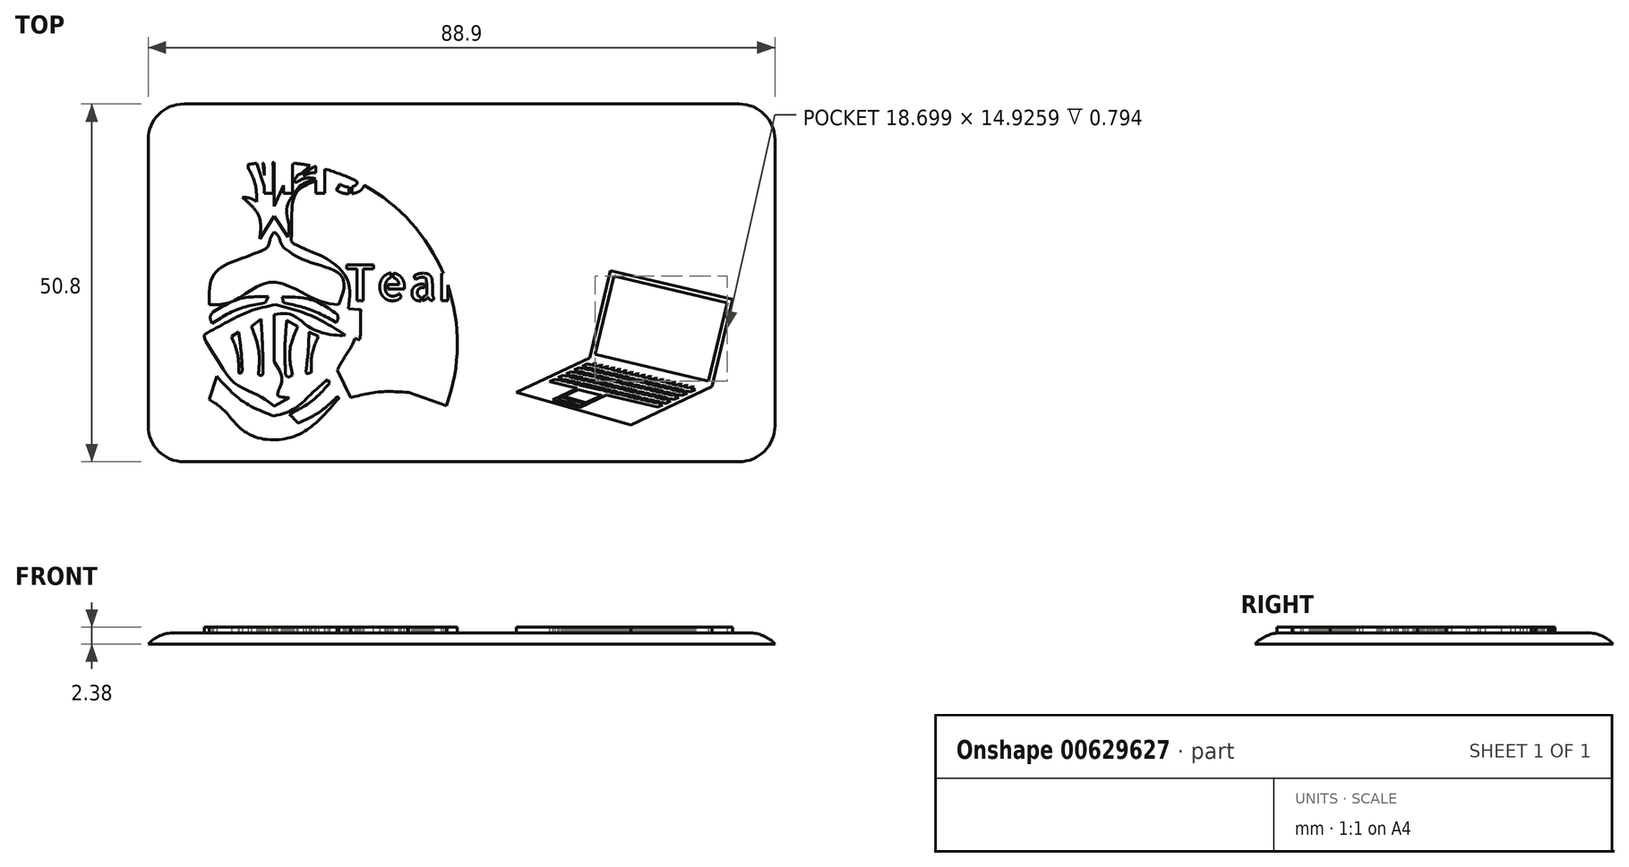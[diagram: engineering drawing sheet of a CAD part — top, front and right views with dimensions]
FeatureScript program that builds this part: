
annotation { "Feature Type Name" : "Feature", "Feature Type Description" : "" }
export const myFeature = defineFeature(function(context is Context, id is Id, definition is map)
    precondition{}
    {
        {
            var Q0;
            Q0=qCreatedBy(makeId("Top.planeOp"),FACE);
            var sketch = newSketch(context, id + "F0", { "sketchPlane" : qUnion([Q0])});
            skLineSegment(sketch, "E0.bottom", {"start": v(-44.45, 25.4) * mm, "end": v(44.45, 25.4) * mm});
            skLineSegment(sketch, "E0.top", {"start": v(-44.45, -25.4) * mm, "end": v(44.45, -25.4) * mm});
            skLineSegment(sketch, "E0.left", {"start": v(-44.45, 25.4) * mm, "end": v(-44.45, -25.4) * mm});
            skLineSegment(sketch, "E0.right", {"start": v(44.45, 25.4) * mm, "end": v(44.45, -25.4) * mm});
            skPoint(sketch, "E0.middle", {"position": v(0, 0) * mm});
            skSolve(sketch);
        }
        {
            var Q0;
            Q0=qSketchRegion(id+"F0",true);
            extrude(context, id + "F1", {"entities" : qUnion([Q0]), "depth" : 1.59 * mm, "offsetDistance" : 25.4 * mm});
        }
        {
            var Q0;
            {var subQ0=sQuery(id+"F0.wireOp",EDGE,"E0.right");var subQ1=sQuery(id+"F0.wireOp",EDGE,"E0.left");var subQ2=sQuery(id+"F0.wireOp",EDGE,"E0.top");var subQ3=sQuery(id+"F0.wireOp",EDGE,"E0.bottom");var subQ4=makeQuery(id+"F1.opExtrude","CAP_FACE",FACE,{"disambiguationData":[OSD([subQ3,subQ2,subQ1,subQ0])],"isStart":false});Q0=makeQuery(id+"F5.boolean.opBoolean","SPLIT",FACE,{"disambiguationData":[TD([makeQuery(id+"F7.boolean.opBoolean","COPY",FACE,{"derivedFrom":makeQuery(id+"F7.opExtrude","SWEPT_FACE",FACE,{"disambiguationData":[OSD([sQuery(id+"F6.wireOp",EDGE,"E188.sketch_text.stroke-0")])]})})])],"derivedFrom":subQ4});}
            var sketch = newSketch(context, id + "F2", { "sketchPlane" : qUnion([Q0])});
            skLineSegment(sketch, "E1", {"start": v(-39.93, 20.88) * mm, "end": v(-39.93, 13.23) * mm});
            skLineSegment(sketch, "E2", {"start": v(-39.93, 20.88) * mm, "end": v(-39.12, 20.88) * mm});
            skLineSegment(sketch, "E3", {"start": v(-37.79, -20.88) * mm, "end": v(-35.63, -20.88) * mm});
            skLineSegment(sketch, "E4.0", {"start": v(-11.09, 20.88) * mm, "end": v(-6.97, 18.68) * mm});
            skLineSegment(sketch, "E4.1", {"start": v(-14.12, 20.88) * mm, "end": v(-16.69, 18.68) * mm});
            skLineSegment(sketch, "E4.13", {"start": v(2.67, -20.88) * mm, "end": v(0.61, -18.26) * mm});
            skLineSegment(sketch, "E4.14", {"start": v(0.36, 11.02) * mm, "end": v(3.83, 4.92) * mm});
            skLineSegment(sketch, "E4.15", {"start": v(0.36, 11.02) * mm, "end": v(-4.42, 10.07) * mm});
            skArc(sketch, "E4.16", {"start": v(-4.42, 10.07) * mm, "mid": v(-5.98, 11.8) * mm, "end": v(-7.68, 13.38) * mm});
            skLineSegment(sketch, "E4.17", {"start": v(-6.97, 18.68) * mm, "end": v(-7.68, 13.38) * mm});
            skLineSegment(sketch, "E4.18", {"start": v(3.83, 4.92) * mm, "end": v(0.61, 1.3) * mm});
            skArc(sketch, "E4.19", {"start": v(1.92, -3.68) * mm, "mid": v(1.38, -1.16) * mm, "end": v(0.61, 1.3) * mm});
            skLineSegment(sketch, "E4.20", {"start": v(6.61, -5.16) * mm, "end": v(1.92, -3.68) * mm});
            skLineSegment(sketch, "E4.21", {"start": v(6.61, -5.16) * mm, "end": v(6.61, -11.77) * mm});
            skLineSegment(sketch, "E4.22", {"start": v(6.61, -11.77) * mm, "end": v(1.92, -13.28) * mm});
            skArc(sketch, "E4.23", {"start": v(0.61, -18.26) * mm, "mid": v(1.38, -15.8) * mm, "end": v(1.92, -13.28) * mm});
            skLineSegment(sketch, "E4.42", {"start": v(-39.12, 20.88) * mm, "end": v(-36.5, 18.68) * mm});
            skArc(sketch, "E4.43", {"start": v(-31.89, 19.94) * mm, "mid": v(-34.22, 19.4) * mm, "end": v(-36.5, 18.68) * mm});
            skLineSegment(sketch, "E4.44", {"start": v(-31.89, 19.94) * mm, "end": v(-31.5, 20.88) * mm});
            skLineSegment(sketch, "E4.46", {"start": v(-21.66, 20.88) * mm, "end": v(-21.3, 19.94) * mm});
            skArc(sketch, "E4.47", {"start": v(-16.69, 18.68) * mm, "mid": v(-18.96, 19.4) * mm, "end": v(-21.3, 19.94) * mm});
            skLineSegment(sketch, "E5.0", {"start": v(-17.63, -12.4) * mm, "end": v(-15.7, -16.29) * mm});
            skFitSpline(sketch, "E5.1", {"points": [v(-7.65, -15.55) * mm, v(-11.69, -15.5) * mm, v(-15.7, -16.29) * mm]});
            skLineSegment(sketch, "E5.2", {"start": v(-7.65, -15.55) * mm, "end": v(-7.5, -15.55) * mm});
            skLineSegment(sketch, "E5.3", {"start": v(-16.04, -3.68) * mm, "end": v(-14.6, -3.8) * mm});
            skFitSpline(sketch, "E5.4", {"points": [v(-14.36, -4.47) * mm, v(-14.33, -4.23) * mm, v(-14.32, -3.82) * mm, v(-14.6, -3.8) * mm]});
            skLineSegment(sketch, "E5.5", {"start": v(-14.36, -4.47) * mm, "end": v(-14.36, -7.44) * mm});
            skFitSpline(sketch, "E5.6", {"points": [v(-15.13, -7.93) * mm, v(-14.83, -7.99) * mm, v(-14.54, -8.08) * mm, v(-14.36, -7.44) * mm]});
            skFitSpline(sketch, "E5.7", {"points": [v(-16.04, -3.68) * mm, v(-16.1, 0.17) * mm, v(-19.42, 3.57) * mm, v(-23.98, 5.7) * mm, v(-24.16, 6.21) * mm]});
            skFitSpline(sketch, "E5.8", {"points": [v(-24.16, 6.21) * mm, v(-24.11, 7.19) * mm, v(-23.98, 11.28) * mm, v(-22.96, 13.3) * mm, v(-19.48, 14.97) * mm]});
            skFitSpline(sketch, "E5.9", {"points": [v(-19.48, 14.97) * mm, v(-20.81, 15.64) * mm, v(-22.46, 15.17) * mm]});
            skFitSpline(sketch, "E5.10", {"points": [v(-17.63, -12.4) * mm, v(-16.8, -10.89) * mm, v(-15.86, -9.46) * mm, v(-15.13, -7.93) * mm]});
            skFitSpline(sketch, "E5.11", {"points": [v(-22.46, 15.17) * mm, v(-21.72, 15.9) * mm, v(-20.87, 16.52) * mm]});
            skArc(sketch, "E5.12", {"start": v(-2.15, -17.45) * mm, "mid": v(-3.8, 3.8) * mm, "end": v(-20.87, 16.52) * mm});
            skLineSegment(sketch, "E5.13", {"start": v(-7.5, -15.55) * mm, "end": v(-2.15, -17.45) * mm});
            skArc(sketch, "E6.0", {"start": v(-31.1, 16.66) * mm, "mid": v(-35.68, 15.36) * mm, "end": v(-39.93, 13.23) * mm});
            skLineSegment(sketch, "E6.2", {"start": v(-38.12, -3.8) * mm, "end": v(-37.08, -3.8) * mm});
            skFitSpline(sketch, "E6.3", {"points": [v(-29.04, 5.91) * mm, v(-32.6, 3.54) * mm, v(-36.03, 3.27) * mm, v(-37.08, -3.8) * mm]});
            skFitSpline(sketch, "E6.4", {"points": [v(-32.5, 12.72) * mm, v(-29.26, 10.64) * mm, v(-29.04, 5.91) * mm]});
            skFitSpline(sketch, "E6.5", {"points": [v(-29.6, 12.07) * mm, v(-30.83, 12.9) * mm, v(-32.5, 12.72) * mm]});
            skFitSpline(sketch, "E6.6", {"points": [v(-38.12, -3.8) * mm, v(-38.46, -3.77) * mm, v(-38.6, -3.99) * mm, v(-38.6, -4.15) * mm]});
            skLineSegment(sketch, "E6.7", {"start": v(-38.6, -7.34) * mm, "end": v(-38.6, -4.15) * mm});
            skFitSpline(sketch, "E6.8", {"points": [v(-31.1, 16.66) * mm, v(-30.26, 15.3) * mm, v(-29.66, 13.77) * mm, v(-29.6, 12.07) * mm]});
            skFitSpline(sketch, "E6.9", {"points": [v(-38.6, -7.34) * mm, v(-38.84, -7.76) * mm, v(-38.04, -8) * mm]});
            skFitSpline(sketch, "E6.10", {"points": [v(-38.04, -8) * mm, v(-36.8, -10.21) * mm, v(-35.5, -12.4) * mm]});
            skLineSegment(sketch, "E6.11", {"start": v(-37.39, -16.29) * mm, "end": v(-35.5, -12.4) * mm});
            skFitSpline(sketch, "E6.12", {"points": [v(-37.39, -16.29) * mm, v(-41.55, -15.61) * mm, v(-45.73, -15.55) * mm]});
            skLineSegment(sketch, "E7.0", {"start": v(-33.08, -20.88) * mm, "end": v(-35.5, -19.2) * mm});
            skLineSegment(sketch, "E7.1", {"start": v(-35.5, -19.2) * mm, "end": v(-35.63, -20.88) * mm});
            skArc(sketch, "E8.1", {"start": v(-3.7, -20.88) * mm, "mid": v(-3.07, -19.66) * mm, "end": v(-2.52, -18.4) * mm});
            skLineSegment(sketch, "E8.2", {"start": v(-16.04, -18.26) * mm, "end": v(-15.47, -20.88) * mm});
            skFitSpline(sketch, "E8.3", {"points": [v(-16.04, -18.26) * mm, v(-16.15, -17.79) * mm, v(-15.43, -17.5) * mm]});
            skLineSegment(sketch, "E8.4", {"start": v(-7.5, -16.6) * mm, "end": v(-15.43, -17.5) * mm});
            skLineSegment(sketch, "E8.6", {"start": v(-2.52, -18.4) * mm, "end": v(-7.5, -16.6) * mm});
            skLineSegment(sketch, "E9.0", {"start": v(-37.39, -17.54) * mm, "end": v(-39.93, -17.25) * mm});
            skLineSegment(sketch, "E9.1", {"start": v(-37.79, -20.88) * mm, "end": v(-37.39, -18.92) * mm});
            skFitSpline(sketch, "E9.3", {"points": [v(-37.39, -17.54) * mm, v(-37.1, -18.3) * mm, v(-37.39, -18.92) * mm]});
            skFitSpline(sketch, "E10.0", {"points": [v(-23.19, -19.91) * mm, v(-20.18, -18.37) * mm, v(-17.6, -16.11) * mm]});
            skFitSpline(sketch, "E10.1", {"points": [v(-23.19, -19.91) * mm, v(-23.5, -19.6) * mm, v(-23.9, -19.16) * mm, v(-24.45, -18.66) * mm]});
            skFitSpline(sketch, "E10.2", {"points": [v(-17.6, -16.11) * mm, v(-17.44, -16.44) * mm, v(-17.63, -16.6) * mm]});
            skFitSpline(sketch, "E10.3", {"points": [v(-18.7, -14.2) * mm, v(-21.24, -16.8) * mm, v(-24.45, -18.66) * mm]});
            skLineSegment(sketch, "E10.4", {"start": v(-18.7, -14.2) * mm, "end": v(-18.94, -13.74) * mm});
            skFitSpline(sketch, "E10.5", {"points": [v(-17.63, -16.6) * mm, v(-19.85, -19.09) * mm, v(-22.95, -21.46) * mm, v(-27.12, -22.28) * mm, v(-31.04, -20.92) * mm, v(-33.86, -17.94) * mm, v(-35.78, -16.6) * mm]});
            skLineSegment(sketch, "E10.6", {"start": v(-34.7, -13.28) * mm, "end": v(-35.78, -16.6) * mm});
            skFitSpline(sketch, "E10.7", {"points": [v(-26.6, -18.92) * mm, v(-31.06, -16.8) * mm, v(-34.7, -13.28) * mm]});
            skFitSpline(sketch, "E10.8", {"points": [v(-18.94, -13.74) * mm, v(-21.29, -15.73) * mm, v(-23.66, -17.85) * mm, v(-26.6, -18.92) * mm]});
            skFitSpline(sketch, "E11.0", {"points": [v(-26.6, -17.54) * mm, v(-28.47, -16.2) * mm, v(-32.14, -14.27) * mm, v(-34.18, -11.66) * mm, v(-36.38, -8.05) * mm, v(-36.5, -7.34) * mm]});
            skLineSegment(sketch, "E11.1", {"start": v(-26.6, -17.54) * mm, "end": v(-24.45, -16.29) * mm});
            skFitSpline(sketch, "E11.2", {"points": [v(-26.34, -3.1) * mm, v(-21.2, -4.73) * mm, v(-16.46, -7.44) * mm]});
            skFitSpline(sketch, "E11.3", {"points": [v(-16.46, -7.44) * mm, v(-17.65, -7.44) * mm, v(-21.16, -6.55) * mm, v(-24.06, -4.55) * mm, v(-26.56, -4.47) * mm]});
            skLineSegment(sketch, "E11.4", {"start": v(-26.56, -11.18) * mm, "end": v(-26.56, -4.47) * mm});
            skFitSpline(sketch, "E11.5", {"points": [v(-36.5, -7.34) * mm, v(-33.28, -5.58) * mm, v(-29.94, -4) * mm, v(-26.34, -3.1) * mm]});
            skFitSpline(sketch, "E11.6", {"points": [v(-26.56, -11.18) * mm, v(-25.5, -14.07) * mm, v(-26.07, -15.95) * mm, v(-24.45, -16.29) * mm]});
            skFitSpline(sketch, "E12.0", {"points": [v(-29.8, -6.2) * mm, v(-28.78, -9.6) * mm, v(-28.81, -13.06) * mm]});
            skLineSegment(sketch, "E12.1", {"start": v(-28.45, -5.16) * mm, "end": v(-29.8, -6.2) * mm});
            skFitSpline(sketch, "E12.2", {"points": [v(-28.17, -12.77) * mm, v(-28.23, -8.96) * mm, v(-28.45, -5.16) * mm]});
            skFitSpline(sketch, "E12.3", {"points": [v(-28.81, -13.06) * mm, v(-28.3, -13.1) * mm, v(-28.17, -12.77) * mm]});
            skFitSpline(sketch, "E13.0", {"points": [v(-31.61, -12.77) * mm, v(-31.3, -12.82) * mm, v(-31.1, -12.4) * mm]});
            skFitSpline(sketch, "E13.1", {"points": [v(-32.64, -7.63) * mm, v(-31.76, -10.15) * mm, v(-31.61, -12.77) * mm]});
            skLineSegment(sketch, "E13.2", {"start": v(-31.61, -6.96) * mm, "end": v(-32.64, -7.63) * mm});
            skFitSpline(sketch, "E13.3", {"points": [v(-31.1, -12.4) * mm, v(-31.28, -9.67) * mm, v(-31.61, -6.96) * mm]});
            skFitSpline(sketch, "E14.0", {"points": [v(-25, -12.77) * mm, v(-24.92, -13.1) * mm, v(-24.52, -13.36) * mm, v(-23.99, -13.06) * mm]});
            skFitSpline(sketch, "E14.1", {"points": [v(-25, -12.77) * mm, v(-25.05, -9.05) * mm, v(-24.8, -5.34) * mm]});
            skLineSegment(sketch, "E14.2", {"start": v(-23.19, -6.2) * mm, "end": v(-24.8, -5.34) * mm});
            skFitSpline(sketch, "E14.3", {"points": [v(-23.99, -13.06) * mm, v(-24.35, -9.62) * mm, v(-23.19, -6.2) * mm]});
            skFitSpline(sketch, "E15.0", {"points": [v(-21.3, -12.77) * mm, v(-21.41, -12.73) * mm, v(-21.9, -12.9) * mm, v(-22.07, -12.52) * mm]});
            skFitSpline(sketch, "E15.1", {"points": [v(-21.3, -12.77) * mm, v(-21.22, -10.15) * mm, v(-20.3, -7.63) * mm]});
            skLineSegment(sketch, "E15.2", {"start": v(-20.3, -7.63) * mm, "end": v(-21.64, -6.96) * mm});
            skFitSpline(sketch, "E15.3", {"points": [v(-22.07, -12.52) * mm, v(-21.76, -9.75) * mm, v(-21.64, -6.96) * mm]});
            skFitSpline(sketch, "E16.0", {"points": [v(-27.86, -2.82) * mm, v(-31.79, -3.78) * mm, v(-35.38, -5.78) * mm]});
            skLineSegment(sketch, "E16.1", {"start": v(-27.86, -2.82) * mm, "end": v(-27.44, -1.99) * mm});
            skFitSpline(sketch, "E16.2", {"points": [v(-27.44, -1.99) * mm, v(-31.46, -2.27) * mm, v(-35.22, -4.15) * mm]});
            skFitSpline(sketch, "E16.3", {"points": [v(-35.38, -5.78) * mm, v(-35.64, -4.85) * mm, v(-35.22, -4.15) * mm]});
            skFitSpline(sketch, "E17.0", {"points": [v(-25.24, -2.82) * mm, v(-21.38, -3.85) * mm, v(-17.74, -5.62) * mm]});
            skLineSegment(sketch, "E17.1", {"start": v(-25.46, -1.99) * mm, "end": v(-25.24, -2.82) * mm});
            skFitSpline(sketch, "E17.2", {"points": [v(-17.63, -4.47) * mm, v(-21.2, -2.44) * mm, v(-25.46, -1.99) * mm]});
            skFitSpline(sketch, "E17.3", {"points": [v(-17.74, -5.62) * mm, v(-17.54, -5.08) * mm, v(-17.63, -4.47) * mm]});
            skLineSegment(sketch, "E18.0", {"start": v(-21.64, 16.53) * mm, "end": v(-21.52, 16.66) * mm});
            skArc(sketch, "E18.1", {"start": v(-21.52, 16.66) * mm, "mid": v(-22.69, 16.85) * mm, "end": v(-23.87, 17) * mm});
            skLineSegment(sketch, "E18.2", {"start": v(-23.87, 17) * mm, "end": v(-26.6, 10.84) * mm});
            skLineSegment(sketch, "E18.3", {"start": v(-26.6, 10.84) * mm, "end": v(-26.6, 17.1) * mm});
            skArc(sketch, "E18.4", {"start": v(-26.6, 17.1) * mm, "mid": v(-27.38, 17.09) * mm, "end": v(-28.17, 17.04) * mm});
            skFitSpline(sketch, "E18.5", {"points": [v(-21.64, 16.53) * mm, v(-22.97, 15.4) * mm, v(-23.04, 15.44) * mm, v(-23.74, 14.42) * mm, v(-23.43, 14.3) * mm]});
            skLineSegment(sketch, "E18.6", {"start": v(-28.17, 17.04) * mm, "end": v(-27.72, 12.88) * mm});
            skLineSegment(sketch, "E18.7", {"start": v(-26.6, 9.5) * mm, "end": v(-24.6, 6.5) * mm});
            skFitSpline(sketch, "E18.8", {"points": [v(-20.66, 14.78) * mm, v(-22.53, 14.03) * mm, v(-23.6, 12.91) * mm, v(-24.83, 10.42) * mm, v(-24.5, 8.42) * mm, v(-24.6, 6.5) * mm]});
            skFitSpline(sketch, "E18.9", {"points": [v(-23.39, 14.3) * mm, v(-22.04, 14.87) * mm, v(-20.66, 14.78) * mm]});
            skLineSegment(sketch, "E18.10", {"start": v(-23.39, 14.3) * mm, "end": v(-23.43, 14.3) * mm});
            skLineSegment(sketch, "E18.11", {"start": v(-28.64, 6.21) * mm, "end": v(-26.6, 9.5) * mm});
            skFitSpline(sketch, "E18.12", {"points": [v(-28.64, 6.21) * mm, v(-28.74, 9.43) * mm, v(-31.1, 12.15) * mm]});
            skFitSpline(sketch, "E18.13", {"points": [v(-31.1, 12.15) * mm, v(-30.03, 12.01) * mm, v(-29.04, 11.5) * mm]});
            skFitSpline(sketch, "E18.14", {"points": [v(-29.04, 11.5) * mm, v(-29.32, 14.22) * mm, v(-30.54, 16.77) * mm]});
            skArc(sketch, "E18.15", {"start": v(-29.04, 16.97) * mm, "mid": v(-29.79, 16.88) * mm, "end": v(-30.54, 16.77) * mm});
            skLineSegment(sketch, "E18.16", {"start": v(-27.72, 12.88) * mm, "end": v(-29.04, 16.97) * mm});
            skFitSpline(sketch, "E19.0", {"points": [v(-35.78, -3.1) * mm, v(-35.06, 1.3) * mm, v(-31.74, 3.25) * mm, v(-28.45, 4.52) * mm]});
            skFitSpline(sketch, "E20.0", {"points": [v(-28.45, 4.52) * mm, v(-27.52, 5.12) * mm, v(-27.11, 6.28) * mm, v(-26.6, 7.24) * mm]});
            skFitSpline(sketch, "E21.0", {"points": [v(-25.15, 4.92) * mm, v(-21.92, 3.09) * mm, v(-16.98, 0.88) * mm, v(-17.42, -3.1) * mm]});
            skFitSpline(sketch, "E21.1", {"points": [v(-26.6, 7.24) * mm, v(-25.96, 6.59) * mm, v(-25.67, 5.71) * mm, v(-25.15, 4.92) * mm]});
            skFitSpline(sketch, "E22.0", {"points": [v(-35.78, -3.1) * mm, v(-32.32, -2.55) * mm, v(-26.97, 0.08) * mm, v(-20.8, -2.33) * mm, v(-17.42, -3.1) * mm]});
            skLineSegment(sketch, "E23.trimOffspring", {"start": v(-39.93, -15.93) * mm, "end": v(-39.93, -17.25) * mm});
            skLineSegment(sketch, "E24.trimOffspring", {"start": v(-33.08, -20.88) * mm, "end": v(-30.2, -20.88) * mm});
            skFitSpline(sketch, "E25.trimOffspring", {"points": [v(-17.63, -16.6) * mm, v(-19.85, -19.09) * mm, v(-22.95, -21.46) * mm, v(-27.12, -22.28) * mm, v(-31.04, -20.92) * mm, v(-33.86, -17.94) * mm, v(-35.78, -16.6) * mm]});
            skLineSegment(sketch, "E26.trimOffspring", {"start": v(-22.9, -20.88) * mm, "end": v(-15.47, -20.88) * mm});
            skLineSegment(sketch, "E27.trimOffspring", {"start": v(-3.7, -20.88) * mm, "end": v(2.67, -20.88) * mm});
            skPoint(sketch, "E28.orphan", {"position": v(87.07, -20.88) * mm});
            skLineSegment(sketch, "E29.trimOffspring", {"start": v(-31.5, 20.88) * mm, "end": v(-21.66, 20.88) * mm});
            skPoint(sketch, "E30.orphan", {"position": v(48.02, 20.88) * mm});
            skLineSegment(sketch, "E31.trimOffspring", {"start": v(-14.12, 20.88) * mm, "end": v(-11.09, 20.88) * mm});
            skSolve(sketch);
        }
        {
            var Q0;
            Q0=qSketchRegion(id+"F2",true);
            extrude(context, id + "F3", {"entities" : qUnion([Q0]), "operationType" : NewBodyOperationType.ADD, "depth" : 0.8 * mm, "offsetDistance" : 25.4 * mm});
        }
        {
            var Q0;
            Q0=makeQuery(id+"F1.opExtrude","CAP_FACE",FACE,{"disambiguationData":[OSD([sQuery(id+"F0.wireOp",EDGE,"E0.bottom"),sQuery(id+"F0.wireOp",EDGE,"E0.top"),sQuery(id+"F0.wireOp",EDGE,"E0.left"),sQuery(id+"F0.wireOp",EDGE,"E0.right")])],"isStart":false});
            var sketch = newSketch(context, id + "F4", { "sketchPlane" : qUnion([Q0])});
            skLineSegment(sketch, "E32", {"start": v(-33.18, -82.37) * mm, "end": v(-27.78, -81.02) * mm});
            skLineSegment(sketch, "E33", {"start": v(24.02, -20.16) * mm, "end": v(35.5, -14.73) * mm});
            skLineSegment(sketch, "E34", {"start": v(35.5, -14.73) * mm, "end": v(38.42, -2.37) * mm});
            skLineSegment(sketch, "E35", {"start": v(38.42, -2.37) * mm, "end": v(21.12, 1.72) * mm});
            skLineSegment(sketch, "E36", {"start": v(21.12, 1.72) * mm, "end": v(18.2, -10.63) * mm});
            skLineSegment(sketch, "E37", {"start": v(18.2, -10.63) * mm, "end": v(35.5, -14.73) * mm});
            skLineSegment(sketch, "E38", {"start": v(18.2, -10.63) * mm, "end": v(7.79, -15.56) * mm});
            skLineSegment(sketch, "E39", {"start": v(7.79, -15.56) * mm, "end": v(24.02, -20.16) * mm});
            skLineSegment(sketch, "E40.0", {"start": v(18.27, -11.3) * mm, "end": v(19.13, -11.5) * mm});
            skLineSegment(sketch, "E40.1", {"start": v(17.83, -11.51) * mm, "end": v(17.12, -11.85) * mm});
            skLineSegment(sketch, "E40.2", {"start": v(13.62, -16.56) * mm, "end": v(15.08, -16.97) * mm});
            skLineSegment(sketch, "E40.3", {"start": v(27.82, -17.66) * mm, "end": v(28.56, -17.31) * mm});
            skLineSegment(sketch, "E41", {"start": v(17.83, -11.51) * mm, "end": v(18.42, -11.65) * mm});
            skLineSegment(sketch, "E42", {"start": v(18.42, -11.65) * mm, "end": v(18.86, -11.44) * mm});
            skPoint(sketch, "E43", {"position": v(17.83, -11.51) * mm});
            skPoint(sketch, "E44", {"position": v(18.27, -11.3) * mm});
            skPoint(sketch, "E45", {"position": v(18.42, -11.65) * mm});
            skPoint(sketch, "E46", {"position": v(18.86, -11.44) * mm});
            skPoint(sketch, "E47.1.0.0", {"position": v(19.13, -11.5) * mm});
            skLineSegment(sketch, "E47.1.0.1", {"start": v(18.7, -11.72) * mm, "end": v(19.28, -11.86) * mm});
            skLineSegment(sketch, "E47.1.0.2", {"start": v(19.28, -11.86) * mm, "end": v(19.72, -11.65) * mm});
            skPoint(sketch, "E47.1.0.3", {"position": v(19.28, -11.86) * mm});
            skPoint(sketch, "E47.1.0.4", {"position": v(19.72, -11.65) * mm});
            skPoint(sketch, "E47.1.0.5", {"position": v(18.7, -11.72) * mm});
            skPoint(sketch, "E47.2.0.0", {"position": v(20, -11.71) * mm});
            skLineSegment(sketch, "E47.2.0.1", {"start": v(19.56, -11.92) * mm, "end": v(20.15, -12.06) * mm});
            skLineSegment(sketch, "E47.2.0.2", {"start": v(20.15, -12.06) * mm, "end": v(20.59, -11.85) * mm});
            skPoint(sketch, "E47.2.0.3", {"position": v(20.15, -12.06) * mm});
            skPoint(sketch, "E47.2.0.4", {"position": v(20.59, -11.85) * mm});
            skPoint(sketch, "E47.2.0.5", {"position": v(19.56, -11.92) * mm});
            skPoint(sketch, "E47.3.0.0", {"position": v(20.86, -11.92) * mm});
            skLineSegment(sketch, "E47.3.0.1", {"start": v(20.42, -12.13) * mm, "end": v(21.01, -12.27) * mm});
            skLineSegment(sketch, "E47.3.0.2", {"start": v(21.01, -12.27) * mm, "end": v(21.45, -12.06) * mm});
            skPoint(sketch, "E47.3.0.3", {"position": v(21.01, -12.27) * mm});
            skPoint(sketch, "E47.3.0.4", {"position": v(21.45, -12.06) * mm});
            skPoint(sketch, "E47.3.0.5", {"position": v(20.42, -12.13) * mm});
            skPoint(sketch, "E47.4.0.0", {"position": v(21.73, -12.12) * mm});
            skLineSegment(sketch, "E47.4.0.1", {"start": v(21.29, -12.33) * mm, "end": v(21.88, -12.47) * mm});
            skLineSegment(sketch, "E47.4.0.2", {"start": v(21.88, -12.47) * mm, "end": v(22.32, -12.26) * mm});
            skPoint(sketch, "E47.4.0.3", {"position": v(21.88, -12.47) * mm});
            skPoint(sketch, "E47.4.0.4", {"position": v(22.32, -12.26) * mm});
            skPoint(sketch, "E47.4.0.5", {"position": v(21.29, -12.33) * mm});
            skPoint(sketch, "E47.5.0.0", {"position": v(22.6, -12.33) * mm});
            skLineSegment(sketch, "E47.5.0.1", {"start": v(22.15, -12.54) * mm, "end": v(22.74, -12.68) * mm});
            skLineSegment(sketch, "E47.5.0.2", {"start": v(22.74, -12.68) * mm, "end": v(23.18, -12.47) * mm});
            skPoint(sketch, "E47.5.0.3", {"position": v(22.74, -12.68) * mm});
            skPoint(sketch, "E47.5.0.4", {"position": v(23.18, -12.47) * mm});
            skPoint(sketch, "E47.5.0.5", {"position": v(22.15, -12.54) * mm});
            skPoint(sketch, "E47.6.0.0", {"position": v(23.46, -12.53) * mm});
            skLineSegment(sketch, "E47.6.0.1", {"start": v(23.02, -12.74) * mm, "end": v(23.6, -12.88) * mm});
            skLineSegment(sketch, "E47.6.0.2", {"start": v(23.6, -12.88) * mm, "end": v(24.05, -12.67) * mm});
            skPoint(sketch, "E47.6.0.3", {"position": v(23.6, -12.88) * mm});
            skPoint(sketch, "E47.6.0.4", {"position": v(24.05, -12.67) * mm});
            skPoint(sketch, "E47.6.0.5", {"position": v(23.02, -12.74) * mm});
            skPoint(sketch, "E47.7.0.0", {"position": v(24.32, -12.74) * mm});
            skLineSegment(sketch, "E47.7.0.1", {"start": v(23.88, -12.95) * mm, "end": v(24.47, -13.09) * mm});
            skLineSegment(sketch, "E47.7.0.2", {"start": v(24.47, -13.09) * mm, "end": v(24.91, -12.88) * mm});
            skPoint(sketch, "E47.7.0.3", {"position": v(24.47, -13.09) * mm});
            skPoint(sketch, "E47.7.0.4", {"position": v(24.91, -12.88) * mm});
            skPoint(sketch, "E47.7.0.5", {"position": v(23.88, -12.95) * mm});
            skPoint(sketch, "E47.8.0.0", {"position": v(25.19, -12.94) * mm});
            skLineSegment(sketch, "E47.8.0.1", {"start": v(24.75, -13.15) * mm, "end": v(25.34, -13.3) * mm});
            skLineSegment(sketch, "E47.8.0.2", {"start": v(25.34, -13.3) * mm, "end": v(25.78, -13.08) * mm});
            skPoint(sketch, "E47.8.0.3", {"position": v(25.34, -13.3) * mm});
            skPoint(sketch, "E47.8.0.4", {"position": v(25.78, -13.08) * mm});
            skPoint(sketch, "E47.8.0.5", {"position": v(24.75, -13.15) * mm});
            skPoint(sketch, "E47.9.0.0", {"position": v(26.05, -13.15) * mm});
            skLineSegment(sketch, "E47.9.0.1", {"start": v(25.61, -13.36) * mm, "end": v(26.2, -13.5) * mm});
            skLineSegment(sketch, "E47.9.0.2", {"start": v(26.2, -13.5) * mm, "end": v(26.64, -13.29) * mm});
            skPoint(sketch, "E47.9.0.3", {"position": v(26.2, -13.5) * mm});
            skPoint(sketch, "E47.9.0.4", {"position": v(26.64, -13.29) * mm});
            skPoint(sketch, "E47.9.0.5", {"position": v(25.61, -13.36) * mm});
            skPoint(sketch, "E47.10.0.0", {"position": v(26.92, -13.35) * mm});
            skLineSegment(sketch, "E47.10.0.1", {"start": v(26.48, -13.56) * mm, "end": v(27.07, -13.7) * mm});
            skLineSegment(sketch, "E47.10.0.2", {"start": v(27.07, -13.7) * mm, "end": v(27.5, -13.5) * mm});
            skPoint(sketch, "E47.10.0.3", {"position": v(27.07, -13.7) * mm});
            skPoint(sketch, "E47.10.0.4", {"position": v(27.5, -13.5) * mm});
            skPoint(sketch, "E47.10.0.5", {"position": v(26.48, -13.56) * mm});
            skPoint(sketch, "E47.11.0.0", {"position": v(27.78, -13.56) * mm});
            skLineSegment(sketch, "E47.11.0.1", {"start": v(27.34, -13.77) * mm, "end": v(27.93, -13.9) * mm});
            skLineSegment(sketch, "E47.11.0.2", {"start": v(27.93, -13.9) * mm, "end": v(28.37, -13.7) * mm});
            skPoint(sketch, "E47.11.0.3", {"position": v(27.93, -13.9) * mm});
            skPoint(sketch, "E47.11.0.4", {"position": v(28.37, -13.7) * mm});
            skPoint(sketch, "E47.11.0.5", {"position": v(27.34, -13.77) * mm});
            skPoint(sketch, "E47.12.0.0", {"position": v(28.65, -13.76) * mm});
            skLineSegment(sketch, "E47.12.0.1", {"start": v(28.2, -13.97) * mm, "end": v(28.8, -14.11) * mm});
            skLineSegment(sketch, "E47.12.0.2", {"start": v(28.8, -14.11) * mm, "end": v(29.24, -13.9) * mm});
            skPoint(sketch, "E47.12.0.3", {"position": v(28.8, -14.11) * mm});
            skPoint(sketch, "E47.12.0.4", {"position": v(29.24, -13.9) * mm});
            skPoint(sketch, "E47.12.0.5", {"position": v(28.2, -13.97) * mm});
            skPoint(sketch, "E47.13.0.0", {"position": v(29.51, -13.97) * mm});
            skLineSegment(sketch, "E47.13.0.1", {"start": v(29.07, -14.18) * mm, "end": v(29.66, -14.32) * mm});
            skLineSegment(sketch, "E47.13.0.2", {"start": v(29.66, -14.32) * mm, "end": v(30.1, -14.1) * mm});
            skPoint(sketch, "E47.13.0.3", {"position": v(29.66, -14.32) * mm});
            skPoint(sketch, "E47.13.0.4", {"position": v(30.1, -14.1) * mm});
            skPoint(sketch, "E47.13.0.5", {"position": v(29.07, -14.18) * mm});
            skPoint(sketch, "E47.14.0.0", {"position": v(30.38, -14.17) * mm});
            skLineSegment(sketch, "E47.14.0.1", {"start": v(29.94, -14.38) * mm, "end": v(30.53, -14.52) * mm});
            skLineSegment(sketch, "E47.14.0.2", {"start": v(30.53, -14.52) * mm, "end": v(30.97, -14.31) * mm});
            skPoint(sketch, "E47.14.0.3", {"position": v(30.53, -14.52) * mm});
            skPoint(sketch, "E47.14.0.4", {"position": v(30.97, -14.31) * mm});
            skPoint(sketch, "E47.14.0.5", {"position": v(29.94, -14.38) * mm});
            skPoint(sketch, "E47.15.0.0", {"position": v(31.24, -14.38) * mm});
            skLineSegment(sketch, "E47.15.0.1", {"start": v(30.8, -14.59) * mm, "end": v(31.4, -14.72) * mm});
            skLineSegment(sketch, "E47.15.0.2", {"start": v(31.4, -14.72) * mm, "end": v(31.84, -14.52) * mm});
            skPoint(sketch, "E47.15.0.3", {"position": v(31.4, -14.72) * mm});
            skPoint(sketch, "E47.15.0.4", {"position": v(31.84, -14.52) * mm});
            skPoint(sketch, "E47.15.0.5", {"position": v(30.8, -14.59) * mm});
            skPoint(sketch, "E47.16.0.0", {"position": v(32.1, -14.58) * mm});
            skLineSegment(sketch, "E47.16.0.1", {"start": v(31.67, -14.79) * mm, "end": v(32.26, -14.93) * mm});
            skLineSegment(sketch, "E47.16.0.2", {"start": v(32.26, -14.93) * mm, "end": v(32.7, -14.72) * mm});
            skPoint(sketch, "E47.16.0.3", {"position": v(32.26, -14.93) * mm});
            skPoint(sketch, "E47.16.0.4", {"position": v(32.7, -14.72) * mm});
            skPoint(sketch, "E47.16.0.5", {"position": v(31.67, -14.79) * mm});
            skPoint(sketch, "E47.17.0.0", {"position": v(32.97, -14.79) * mm});
            skLineSegment(sketch, "E47.17.0.1", {"start": v(32.53, -15) * mm, "end": v(33.12, -15.13) * mm});
            skPoint(sketch, "E47.17.0.3", {"position": v(33.12, -15.13) * mm});
            skPoint(sketch, "E47.17.0.4", {"position": v(33.57, -14.93) * mm});
            skPoint(sketch, "E47.17.0.5", {"position": v(32.53, -15) * mm});
            skLineSegment(sketch, "E47.direction1", {"start": v(18.86, -11.44) * mm, "end": v(19.13, -11.5) * mm, "construction": true});
            skLineSegment(sketch, "E48", {"start": v(18.7, -11.72) * mm, "end": v(19.13, -11.5) * mm});
            skLineSegment(sketch, "E49", {"start": v(19.56, -11.92) * mm, "end": v(20, -11.71) * mm});
            skLineSegment(sketch, "E50", {"start": v(20.42, -12.13) * mm, "end": v(20.86, -11.92) * mm});
            skLineSegment(sketch, "E51", {"start": v(21.29, -12.33) * mm, "end": v(21.73, -12.12) * mm});
            skLineSegment(sketch, "E52", {"start": v(22.15, -12.54) * mm, "end": v(22.6, -12.33) * mm});
            skLineSegment(sketch, "E53", {"start": v(23.02, -12.74) * mm, "end": v(23.46, -12.53) * mm});
            skLineSegment(sketch, "E54", {"start": v(23.88, -12.95) * mm, "end": v(24.32, -12.74) * mm});
            skLineSegment(sketch, "E55", {"start": v(24.75, -13.15) * mm, "end": v(25.19, -12.94) * mm});
            skLineSegment(sketch, "E56", {"start": v(25.61, -13.36) * mm, "end": v(26.05, -13.15) * mm});
            skLineSegment(sketch, "E57", {"start": v(26.48, -13.56) * mm, "end": v(26.92, -13.35) * mm});
            skLineSegment(sketch, "E58", {"start": v(27.34, -13.77) * mm, "end": v(27.78, -13.56) * mm});
            skLineSegment(sketch, "E59", {"start": v(28.2, -13.97) * mm, "end": v(28.65, -13.76) * mm});
            skLineSegment(sketch, "E60", {"start": v(29.07, -14.18) * mm, "end": v(29.51, -13.97) * mm});
            skLineSegment(sketch, "E61", {"start": v(29.94, -14.38) * mm, "end": v(30.38, -14.17) * mm});
            skLineSegment(sketch, "E62", {"start": v(30.8, -14.59) * mm, "end": v(31.24, -14.38) * mm});
            skLineSegment(sketch, "E63", {"start": v(31.67, -14.79) * mm, "end": v(32.1, -14.58) * mm});
            skLineSegment(sketch, "E64", {"start": v(32.53, -15) * mm, "end": v(32.97, -14.79) * mm});
            skLineSegment(sketch, "E65", {"start": v(33.12, -15.13) * mm, "end": v(33.15, -15.14) * mm});
            skPoint(sketch, "E66.1.0.0", {"position": v(21.6, -13.22) * mm});
            skPoint(sketch, "E66.1.0.1", {"position": v(21.17, -12.8) * mm});
            skLineSegment(sketch, "E66.1.0.2", {"start": v(23.6, -13.7) * mm, "end": v(24.2, -13.83) * mm});
            skPoint(sketch, "E66.1.0.3", {"position": v(18.13, -12.4) * mm});
            skPoint(sketch, "E66.1.0.4", {"position": v(25.06, -14.04) * mm});
            skPoint(sketch, "E66.1.0.5", {"position": v(17.27, -12.2) * mm});
            skPoint(sketch, "E66.1.0.6", {"position": v(26.2, -14.3) * mm});
            skPoint(sketch, "E66.1.0.7", {"position": v(19.27, -12.67) * mm});
            skPoint(sketch, "E66.1.0.8", {"position": v(22.73, -13.5) * mm});
            skPoint(sketch, "E66.1.0.9", {"position": v(21, -13.08) * mm});
            skPoint(sketch, "E66.1.0.10", {"position": v(17.54, -12.26) * mm});
            skLineSegment(sketch, "E66.1.0.11", {"start": v(20.14, -12.88) * mm, "end": v(20.73, -13.02) * mm});
            skLineSegment(sketch, "E66.1.0.12", {"start": v(22.73, -13.5) * mm, "end": v(23.33, -13.63) * mm});
            skPoint(sketch, "E66.1.0.13", {"position": v(20.58, -12.67) * mm});
            skPoint(sketch, "E66.1.0.14", {"position": v(24.04, -13.49) * mm});
            skPoint(sketch, "E66.1.0.15", {"position": v(24.2, -13.83) * mm});
            skPoint(sketch, "E66.1.0.16", {"position": v(16.68, -12.06) * mm});
            skLineSegment(sketch, "E66.1.0.17", {"start": v(24.46, -13.9) * mm, "end": v(24.9, -13.7) * mm});
            skLineSegment(sketch, "E66.1.0.18", {"start": v(21.87, -13.29) * mm, "end": v(22.46, -13.43) * mm});
            skPoint(sketch, "E66.1.0.19", {"position": v(18.58, -12.2) * mm});
            skPoint(sketch, "E66.1.0.20", {"position": v(22.04, -13.01) * mm});
            skPoint(sketch, "E66.1.0.21", {"position": v(24.46, -13.9) * mm});
            skPoint(sketch, "E66.1.0.22", {"position": v(20.3, -12.6) * mm});
            skPoint(sketch, "E66.1.0.23", {"position": v(19.44, -12.4) * mm});
            skPoint(sketch, "E66.1.0.24", {"position": v(23.77, -13.42) * mm});
            skLineSegment(sketch, "E66.1.0.25", {"start": v(19.27, -12.67) * mm, "end": v(19.86, -12.81) * mm});
            skPoint(sketch, "E66.1.0.26", {"position": v(22.9, -13.22) * mm});
            skPoint(sketch, "E66.1.0.27", {"position": v(18.85, -12.26) * mm});
            skPoint(sketch, "E66.1.0.28", {"position": v(22.31, -13.08) * mm});
            skPoint(sketch, "E66.1.0.29", {"position": v(19, -12.6) * mm});
            skPoint(sketch, "E66.1.0.30", {"position": v(22.46, -13.43) * mm});
            skLineSegment(sketch, "E66.1.0.31", {"start": v(24.2, -13.83) * mm, "end": v(24.63, -13.63) * mm});
            skPoint(sketch, "E66.1.0.32", {"position": v(25.92, -14.24) * mm});
            skLineSegment(sketch, "E66.1.0.33", {"start": v(24.46, -13.9) * mm, "end": v(25.06, -14.04) * mm});
            skPoint(sketch, "E66.1.0.34", {"position": v(20.73, -13.02) * mm});
            skPoint(sketch, "E66.1.0.35", {"position": v(18.4, -12.47) * mm});
            skPoint(sketch, "E66.1.0.36", {"position": v(21.87, -13.29) * mm});
            skLineSegment(sketch, "E66.1.0.37", {"start": v(18.4, -12.47) * mm, "end": v(19, -12.6) * mm});
            skLineSegment(sketch, "E66.1.0.38", {"start": v(21, -13.08) * mm, "end": v(21.6, -13.22) * mm});
            skPoint(sketch, "E66.1.0.39", {"position": v(25.33, -14.1) * mm});
            skLineSegment(sketch, "E66.1.0.40", {"start": v(17.54, -12.26) * mm, "end": v(18.13, -12.4) * mm});
            skLineSegment(sketch, "E66.1.0.41", {"start": v(25.33, -14.1) * mm, "end": v(25.92, -14.24) * mm});
            skPoint(sketch, "E66.1.0.42", {"position": v(21.45, -12.87) * mm});
            skPoint(sketch, "E66.1.0.43", {"position": v(19.86, -12.81) * mm});
            skPoint(sketch, "E66.1.0.44", {"position": v(19.72, -12.46) * mm});
            skPoint(sketch, "E66.1.0.45", {"position": v(23.18, -13.28) * mm});
            skPoint(sketch, "E66.1.0.46", {"position": v(20.14, -12.88) * mm});
            skPoint(sketch, "E66.1.0.47", {"position": v(23.33, -13.63) * mm});
            skPoint(sketch, "E66.1.0.48", {"position": v(23.6, -13.7) * mm});
            skPoint(sketch, "E66.1.0.49", {"position": v(17.99, -12.05) * mm});
            skPoint(sketch, "E66.1.0.50", {"position": v(17.12, -11.85) * mm});
            skPoint(sketch, "E66.1.0.51", {"position": v(17.71, -11.99) * mm});
            skLineSegment(sketch, "E66.1.0.52", {"start": v(22.46, -13.43) * mm, "end": v(22.9, -13.22) * mm});
            skPoint(sketch, "E66.1.0.53", {"position": v(26.36, -14.04) * mm});
            skLineSegment(sketch, "E66.1.0.54", {"start": v(18.4, -12.47) * mm, "end": v(18.85, -12.26) * mm});
            skLineSegment(sketch, "E66.1.0.55", {"start": v(19, -12.6) * mm, "end": v(19.44, -12.4) * mm});
            skLineSegment(sketch, "E66.1.0.56", {"start": v(17.54, -12.26) * mm, "end": v(17.99, -12.05) * mm});
            skLineSegment(sketch, "E66.1.0.57", {"start": v(22.73, -13.5) * mm, "end": v(23.18, -13.28) * mm});
            skLineSegment(sketch, "E66.1.0.58", {"start": v(20.73, -13.02) * mm, "end": v(21.17, -12.8) * mm});
            skLineSegment(sketch, "E66.1.0.59", {"start": v(17.27, -12.2) * mm, "end": v(17.71, -11.99) * mm});
            skLineSegment(sketch, "E66.1.0.60", {"start": v(19.86, -12.81) * mm, "end": v(20.3, -12.6) * mm});
            skLineSegment(sketch, "E66.1.0.61", {"start": v(21, -13.08) * mm, "end": v(21.45, -12.87) * mm});
            skLineSegment(sketch, "E66.1.0.62", {"start": v(23.33, -13.63) * mm, "end": v(23.77, -13.42) * mm});
            skLineSegment(sketch, "E66.1.0.63", {"start": v(20.14, -12.88) * mm, "end": v(20.58, -12.67) * mm});
            skLineSegment(sketch, "E66.1.0.64", {"start": v(19.27, -12.67) * mm, "end": v(19.72, -12.46) * mm});
            skLineSegment(sketch, "E66.1.0.65", {"start": v(21.87, -13.29) * mm, "end": v(22.31, -13.08) * mm});
            skLineSegment(sketch, "E66.1.0.66", {"start": v(18.13, -12.4) * mm, "end": v(18.58, -12.2) * mm});
            skLineSegment(sketch, "E66.1.0.67", {"start": v(23.6, -13.7) * mm, "end": v(24.04, -13.49) * mm});
            skLineSegment(sketch, "E66.1.0.68", {"start": v(21.6, -13.22) * mm, "end": v(22.04, -13.01) * mm});
            skPoint(sketch, "E66.1.0.69", {"position": v(26.64, -14.1) * mm});
            skLineSegment(sketch, "E66.1.0.70", {"start": v(16.68, -12.06) * mm, "end": v(17.27, -12.2) * mm});
            skPoint(sketch, "E66.1.0.71", {"position": v(24.63, -13.63) * mm});
            skPoint(sketch, "E66.1.0.72", {"position": v(24.9, -13.7) * mm});
            skLineSegment(sketch, "E66.1.0.73", {"start": v(25.06, -14.04) * mm, "end": v(25.5, -13.83) * mm});
            skPoint(sketch, "E66.1.0.74", {"position": v(25.5, -13.83) * mm});
            skPoint(sketch, "E66.1.0.75", {"position": v(25.77, -13.9) * mm});
            skLineSegment(sketch, "E66.1.0.76", {"start": v(25.33, -14.1) * mm, "end": v(25.77, -13.9) * mm});
            skLineSegment(sketch, "E66.1.0.77", {"start": v(25.92, -14.24) * mm, "end": v(26.36, -14.04) * mm});
            skLineSegment(sketch, "E66.1.0.78", {"start": v(26.2, -14.3) * mm, "end": v(26.64, -14.1) * mm});
            skLineSegment(sketch, "E66.1.0.79", {"start": v(26.2, -14.3) * mm, "end": v(26.79, -14.45) * mm});
            skLineSegment(sketch, "E66.1.0.80", {"start": v(26.79, -14.45) * mm, "end": v(27.23, -14.24) * mm});
            skLineSegment(sketch, "E66.1.0.81", {"start": v(27.06, -14.51) * mm, "end": v(27.5, -14.3) * mm});
            skLineSegment(sketch, "E66.1.0.82", {"start": v(27.06, -14.51) * mm, "end": v(27.65, -14.65) * mm});
            skLineSegment(sketch, "E66.1.0.83", {"start": v(27.65, -14.65) * mm, "end": v(28.1, -14.44) * mm});
            skPoint(sketch, "E66.1.0.84", {"position": v(27.65, -14.65) * mm});
            skPoint(sketch, "E66.1.0.85", {"position": v(27.06, -14.51) * mm});
            skPoint(sketch, "E66.1.0.86", {"position": v(26.79, -14.45) * mm});
            skPoint(sketch, "E66.1.0.87", {"position": v(27.23, -14.24) * mm});
            skPoint(sketch, "E66.1.0.88", {"position": v(27.5, -14.3) * mm});
            skPoint(sketch, "E66.1.0.89", {"position": v(28.1, -14.44) * mm});
            skPoint(sketch, "E66.1.0.90", {"position": v(28.96, -14.65) * mm});
            skPoint(sketch, "E66.1.0.91", {"position": v(29.66, -15.13) * mm});
            skLineSegment(sketch, "E66.1.0.92", {"start": v(27.92, -14.72) * mm, "end": v(28.37, -14.5) * mm});
            skLineSegment(sketch, "E66.1.0.93", {"start": v(30.52, -15.33) * mm, "end": v(31.11, -15.47) * mm});
            skLineSegment(sketch, "E66.1.0.94", {"start": v(29.38, -15.06) * mm, "end": v(29.82, -14.85) * mm});
            skLineSegment(sketch, "E66.1.0.95", {"start": v(29.66, -15.13) * mm, "end": v(30.25, -15.27) * mm});
            skPoint(sketch, "E66.1.0.96", {"position": v(31.39, -15.54) * mm});
            skLineSegment(sketch, "E66.1.0.97", {"start": v(30.25, -15.27) * mm, "end": v(30.69, -15.06) * mm});
            skPoint(sketch, "E66.1.0.98", {"position": v(29.23, -14.71) * mm});
            skPoint(sketch, "E66.1.0.99", {"position": v(29.82, -14.85) * mm});
            skPoint(sketch, "E66.1.0.100", {"position": v(29.38, -15.06) * mm});
            skPoint(sketch, "E66.1.0.101", {"position": v(31.11, -15.47) * mm});
            skLineSegment(sketch, "E66.1.0.102", {"start": v(30.52, -15.33) * mm, "end": v(30.96, -15.12) * mm});
            skLineSegment(sketch, "E66.1.0.103", {"start": v(31.39, -15.54) * mm, "end": v(31.98, -15.68) * mm});
            skLineSegment(sketch, "E66.1.0.104", {"start": v(28.52, -14.86) * mm, "end": v(28.96, -14.65) * mm});
            skLineSegment(sketch, "E66.1.0.105", {"start": v(31.39, -15.54) * mm, "end": v(31.83, -15.33) * mm});
            skLineSegment(sketch, "E66.1.0.106", {"start": v(31.11, -15.47) * mm, "end": v(31.55, -15.26) * mm});
            skLineSegment(sketch, "E66.1.0.107", {"start": v(28.79, -14.92) * mm, "end": v(29.23, -14.71) * mm});
            skLineSegment(sketch, "E66.1.0.108", {"start": v(29.66, -15.13) * mm, "end": v(30.1, -14.92) * mm});
            skPoint(sketch, "E66.1.0.109", {"position": v(28.37, -14.5) * mm});
            skPoint(sketch, "E66.1.0.110", {"position": v(30.1, -14.92) * mm});
            skPoint(sketch, "E66.1.0.111", {"position": v(30.25, -15.27) * mm});
            skPoint(sketch, "E66.1.0.112", {"position": v(30.52, -15.33) * mm});
            skLineSegment(sketch, "E66.1.0.113", {"start": v(28.79, -14.92) * mm, "end": v(29.38, -15.06) * mm});
            skPoint(sketch, "E66.1.0.114", {"position": v(28.79, -14.92) * mm});
            skPoint(sketch, "E66.1.0.115", {"position": v(28.52, -14.86) * mm});
            skLineSegment(sketch, "E66.1.0.116", {"start": v(27.92, -14.72) * mm, "end": v(28.52, -14.86) * mm});
            skPoint(sketch, "E66.1.0.117", {"position": v(27.92, -14.72) * mm});
            skPoint(sketch, "E66.1.0.118", {"position": v(30.69, -15.06) * mm});
            skPoint(sketch, "E66.1.0.119", {"position": v(30.96, -15.12) * mm});
            skPoint(sketch, "E66.1.0.120", {"position": v(31.55, -15.26) * mm});
            skPoint(sketch, "E66.1.0.121", {"position": v(31.83, -15.33) * mm});
            skPoint(sketch, "E66.1.0.122", {"position": v(31.98, -15.68) * mm});
            skPoint(sketch, "E66.1.0.123", {"position": v(32.42, -15.47) * mm});
            skPoint(sketch, "E66.2.0.0", {"position": v(20.45, -13.76) * mm});
            skPoint(sketch, "E66.2.0.1", {"position": v(20.02, -13.35) * mm});
            skLineSegment(sketch, "E66.2.0.2", {"start": v(22.45, -14.24) * mm, "end": v(23.04, -14.38) * mm});
            skPoint(sketch, "E66.2.0.3", {"position": v(16.99, -12.94) * mm});
            skPoint(sketch, "E66.2.0.4", {"position": v(23.9, -14.58) * mm});
            skPoint(sketch, "E66.2.0.5", {"position": v(16.12, -12.74) * mm});
            skPoint(sketch, "E66.2.0.6", {"position": v(25.05, -14.85) * mm});
            skPoint(sketch, "E66.2.0.7", {"position": v(18.13, -13.21) * mm});
            skPoint(sketch, "E66.2.0.8", {"position": v(21.59, -14.03) * mm});
            skPoint(sketch, "E66.2.0.9", {"position": v(19.86, -13.62) * mm});
            skPoint(sketch, "E66.2.0.10", {"position": v(16.4, -12.8) * mm});
            skLineSegment(sketch, "E66.2.0.11", {"start": v(19, -13.42) * mm, "end": v(19.58, -13.56) * mm});
            skLineSegment(sketch, "E66.2.0.12", {"start": v(21.59, -14.03) * mm, "end": v(22.18, -14.17) * mm});
            skPoint(sketch, "E66.2.0.13", {"position": v(19.43, -13.21) * mm});
            skPoint(sketch, "E66.2.0.14", {"position": v(22.9, -14.03) * mm});
            skPoint(sketch, "E66.2.0.15", {"position": v(23.04, -14.38) * mm});
            skPoint(sketch, "E66.2.0.16", {"position": v(15.53, -12.6) * mm});
            skLineSegment(sketch, "E66.2.0.17", {"start": v(23.32, -14.44) * mm, "end": v(23.76, -14.23) * mm});
            skLineSegment(sketch, "E66.2.0.18", {"start": v(20.72, -13.83) * mm, "end": v(21.31, -13.97) * mm});
            skPoint(sketch, "E66.2.0.19", {"position": v(17.43, -12.74) * mm});
            skPoint(sketch, "E66.2.0.20", {"position": v(20.89, -13.55) * mm});
            skPoint(sketch, "E66.2.0.21", {"position": v(23.32, -14.44) * mm});
            skPoint(sketch, "E66.2.0.22", {"position": v(19.16, -13.15) * mm});
            skPoint(sketch, "E66.2.0.23", {"position": v(18.3, -12.94) * mm});
            skPoint(sketch, "E66.2.0.24", {"position": v(22.62, -13.96) * mm});
            skLineSegment(sketch, "E66.2.0.25", {"start": v(18.13, -13.21) * mm, "end": v(18.72, -13.35) * mm});
            skPoint(sketch, "E66.2.0.26", {"position": v(21.75, -13.76) * mm});
            skPoint(sketch, "E66.2.0.27", {"position": v(17.7, -12.8) * mm});
            skPoint(sketch, "E66.2.0.28", {"position": v(21.16, -13.62) * mm});
            skPoint(sketch, "E66.2.0.29", {"position": v(17.85, -13.15) * mm});
            skPoint(sketch, "E66.2.0.30", {"position": v(21.31, -13.97) * mm});
            skLineSegment(sketch, "E66.2.0.31", {"start": v(23.04, -14.38) * mm, "end": v(23.48, -14.17) * mm});
            skPoint(sketch, "E66.2.0.32", {"position": v(24.77, -14.79) * mm});
            skLineSegment(sketch, "E66.2.0.33", {"start": v(23.32, -14.44) * mm, "end": v(23.9, -14.58) * mm});
            skPoint(sketch, "E66.2.0.34", {"position": v(19.58, -13.56) * mm});
            skPoint(sketch, "E66.2.0.35", {"position": v(17.26, -13) * mm});
            skPoint(sketch, "E66.2.0.36", {"position": v(20.72, -13.83) * mm});
            skLineSegment(sketch, "E66.2.0.37", {"start": v(17.26, -13) * mm, "end": v(17.85, -13.15) * mm});
            skLineSegment(sketch, "E66.2.0.38", {"start": v(19.86, -13.62) * mm, "end": v(20.45, -13.76) * mm});
            skPoint(sketch, "E66.2.0.39", {"position": v(24.18, -14.65) * mm});
            skLineSegment(sketch, "E66.2.0.40", {"start": v(16.4, -12.8) * mm, "end": v(16.99, -12.94) * mm});
            skLineSegment(sketch, "E66.2.0.41", {"start": v(24.18, -14.65) * mm, "end": v(24.77, -14.79) * mm});
            skPoint(sketch, "E66.2.0.42", {"position": v(20.3, -13.41) * mm});
            skPoint(sketch, "E66.2.0.43", {"position": v(18.72, -13.35) * mm});
            skPoint(sketch, "E66.2.0.44", {"position": v(18.57, -13) * mm});
            skPoint(sketch, "E66.2.0.45", {"position": v(22.03, -13.82) * mm});
            skPoint(sketch, "E66.2.0.46", {"position": v(19, -13.42) * mm});
            skPoint(sketch, "E66.2.0.47", {"position": v(22.18, -14.17) * mm});
            skPoint(sketch, "E66.2.0.48", {"position": v(22.45, -14.24) * mm});
            skPoint(sketch, "E66.2.0.49", {"position": v(16.84, -12.6) * mm});
            skPoint(sketch, "E66.2.0.50", {"position": v(15.97, -12.4) * mm});
            skPoint(sketch, "E66.2.0.51", {"position": v(16.56, -12.53) * mm});
            skLineSegment(sketch, "E66.2.0.52", {"start": v(21.31, -13.97) * mm, "end": v(21.75, -13.76) * mm});
            skPoint(sketch, "E66.2.0.53", {"position": v(25.21, -14.58) * mm});
            skLineSegment(sketch, "E66.2.0.54", {"start": v(17.26, -13) * mm, "end": v(17.7, -12.8) * mm});
            skLineSegment(sketch, "E66.2.0.55", {"start": v(17.85, -13.15) * mm, "end": v(18.3, -12.94) * mm});
            skLineSegment(sketch, "E66.2.0.56", {"start": v(16.4, -12.8) * mm, "end": v(16.84, -12.6) * mm});
            skLineSegment(sketch, "E66.2.0.57", {"start": v(21.59, -14.03) * mm, "end": v(22.03, -13.82) * mm});
            skLineSegment(sketch, "E66.2.0.58", {"start": v(19.58, -13.56) * mm, "end": v(20.02, -13.35) * mm});
            skLineSegment(sketch, "E66.2.0.59", {"start": v(16.12, -12.74) * mm, "end": v(16.56, -12.53) * mm});
            skLineSegment(sketch, "E66.2.0.60", {"start": v(18.72, -13.35) * mm, "end": v(19.16, -13.15) * mm});
            skLineSegment(sketch, "E66.2.0.61", {"start": v(19.86, -13.62) * mm, "end": v(20.3, -13.41) * mm});
            skLineSegment(sketch, "E66.2.0.62", {"start": v(22.18, -14.17) * mm, "end": v(22.62, -13.96) * mm});
            skLineSegment(sketch, "E66.2.0.63", {"start": v(19, -13.42) * mm, "end": v(19.43, -13.21) * mm});
            skLineSegment(sketch, "E66.2.0.64", {"start": v(18.13, -13.21) * mm, "end": v(18.57, -13) * mm});
            skLineSegment(sketch, "E66.2.0.65", {"start": v(20.72, -13.83) * mm, "end": v(21.16, -13.62) * mm});
            skLineSegment(sketch, "E66.2.0.66", {"start": v(16.99, -12.94) * mm, "end": v(17.43, -12.74) * mm});
            skLineSegment(sketch, "E66.2.0.67", {"start": v(22.45, -14.24) * mm, "end": v(22.9, -14.03) * mm});
            skLineSegment(sketch, "E66.2.0.68", {"start": v(20.45, -13.76) * mm, "end": v(20.89, -13.55) * mm});
            skPoint(sketch, "E66.2.0.69", {"position": v(25.49, -14.64) * mm});
            skLineSegment(sketch, "E66.2.0.70", {"start": v(15.53, -12.6) * mm, "end": v(16.12, -12.74) * mm});
            skPoint(sketch, "E66.2.0.71", {"position": v(23.48, -14.17) * mm});
            skPoint(sketch, "E66.2.0.72", {"position": v(23.76, -14.23) * mm});
            skLineSegment(sketch, "E66.2.0.73", {"start": v(23.9, -14.58) * mm, "end": v(24.35, -14.37) * mm});
            skPoint(sketch, "E66.2.0.74", {"position": v(24.35, -14.37) * mm});
            skPoint(sketch, "E66.2.0.75", {"position": v(24.62, -14.44) * mm});
            skLineSegment(sketch, "E66.2.0.76", {"start": v(24.18, -14.65) * mm, "end": v(24.62, -14.44) * mm});
            skLineSegment(sketch, "E66.2.0.77", {"start": v(24.77, -14.79) * mm, "end": v(25.21, -14.58) * mm});
            skLineSegment(sketch, "E66.2.0.78", {"start": v(25.05, -14.85) * mm, "end": v(25.49, -14.64) * mm});
            skLineSegment(sketch, "E66.2.0.79", {"start": v(25.05, -14.85) * mm, "end": v(25.64, -15) * mm});
            skLineSegment(sketch, "E66.2.0.80", {"start": v(25.64, -15) * mm, "end": v(26.08, -14.78) * mm});
            skLineSegment(sketch, "E66.2.0.81", {"start": v(25.91, -15.06) * mm, "end": v(26.35, -14.85) * mm});
            skLineSegment(sketch, "E66.2.0.82", {"start": v(25.91, -15.06) * mm, "end": v(26.5, -15.2) * mm});
            skLineSegment(sketch, "E66.2.0.83", {"start": v(26.5, -15.2) * mm, "end": v(26.94, -14.99) * mm});
            skPoint(sketch, "E66.2.0.84", {"position": v(26.5, -15.2) * mm});
            skPoint(sketch, "E66.2.0.85", {"position": v(25.91, -15.06) * mm});
            skPoint(sketch, "E66.2.0.86", {"position": v(25.64, -15) * mm});
            skPoint(sketch, "E66.2.0.87", {"position": v(26.08, -14.78) * mm});
            skPoint(sketch, "E66.2.0.88", {"position": v(26.35, -14.85) * mm});
            skPoint(sketch, "E66.2.0.89", {"position": v(26.94, -14.99) * mm});
            skPoint(sketch, "E66.2.0.90", {"position": v(27.8, -15.2) * mm});
            skPoint(sketch, "E66.2.0.91", {"position": v(28.5, -15.67) * mm});
            skLineSegment(sketch, "E66.2.0.92", {"start": v(26.78, -15.26) * mm, "end": v(27.22, -15.05) * mm});
            skLineSegment(sketch, "E66.2.0.93", {"start": v(29.37, -15.88) * mm, "end": v(29.96, -16.02) * mm});
            skLineSegment(sketch, "E66.2.0.94", {"start": v(28.23, -15.6) * mm, "end": v(28.67, -15.4) * mm});
            skLineSegment(sketch, "E66.2.0.95", {"start": v(28.5, -15.67) * mm, "end": v(29.1, -15.81) * mm});
            skPoint(sketch, "E66.2.0.96", {"position": v(30.24, -16.08) * mm});
            skLineSegment(sketch, "E66.2.0.97", {"start": v(29.1, -15.81) * mm, "end": v(29.54, -15.6) * mm});
            skPoint(sketch, "E66.2.0.98", {"position": v(28.08, -15.26) * mm});
            skPoint(sketch, "E66.2.0.99", {"position": v(28.67, -15.4) * mm});
            skPoint(sketch, "E66.2.0.100", {"position": v(28.23, -15.6) * mm});
            skPoint(sketch, "E66.2.0.101", {"position": v(29.96, -16.02) * mm});
            skLineSegment(sketch, "E66.2.0.102", {"start": v(29.37, -15.88) * mm, "end": v(29.81, -15.67) * mm});
            skLineSegment(sketch, "E66.2.0.103", {"start": v(30.24, -16.08) * mm, "end": v(30.83, -16.22) * mm});
            skLineSegment(sketch, "E66.2.0.104", {"start": v(27.37, -15.4) * mm, "end": v(27.8, -15.2) * mm});
            skLineSegment(sketch, "E66.2.0.105", {"start": v(30.24, -16.08) * mm, "end": v(30.68, -15.87) * mm});
            skLineSegment(sketch, "E66.2.0.106", {"start": v(29.96, -16.02) * mm, "end": v(30.4, -15.8) * mm});
            skLineSegment(sketch, "E66.2.0.107", {"start": v(27.64, -15.47) * mm, "end": v(28.08, -15.26) * mm});
            skLineSegment(sketch, "E66.2.0.108", {"start": v(28.5, -15.67) * mm, "end": v(28.95, -15.46) * mm});
            skPoint(sketch, "E66.2.0.109", {"position": v(27.22, -15.05) * mm});
            skPoint(sketch, "E66.2.0.110", {"position": v(28.95, -15.46) * mm});
            skPoint(sketch, "E66.2.0.111", {"position": v(29.1, -15.81) * mm});
            skPoint(sketch, "E66.2.0.112", {"position": v(29.37, -15.88) * mm});
            skLineSegment(sketch, "E66.2.0.113", {"start": v(27.64, -15.47) * mm, "end": v(28.23, -15.6) * mm});
            skPoint(sketch, "E66.2.0.114", {"position": v(27.64, -15.47) * mm});
            skPoint(sketch, "E66.2.0.115", {"position": v(27.37, -15.4) * mm});
            skLineSegment(sketch, "E66.2.0.116", {"start": v(26.78, -15.26) * mm, "end": v(27.37, -15.4) * mm});
            skPoint(sketch, "E66.2.0.117", {"position": v(26.78, -15.26) * mm});
            skPoint(sketch, "E66.2.0.118", {"position": v(29.54, -15.6) * mm});
            skPoint(sketch, "E66.2.0.119", {"position": v(29.81, -15.67) * mm});
            skPoint(sketch, "E66.2.0.120", {"position": v(30.4, -15.8) * mm});
            skPoint(sketch, "E66.2.0.121", {"position": v(30.68, -15.87) * mm});
            skPoint(sketch, "E66.2.0.122", {"position": v(30.83, -16.22) * mm});
            skPoint(sketch, "E66.2.0.123", {"position": v(31.27, -16.01) * mm});
            skPoint(sketch, "E66.3.0.0", {"position": v(19.3, -14.3) * mm});
            skPoint(sketch, "E66.3.0.1", {"position": v(18.88, -13.9) * mm});
            skLineSegment(sketch, "E66.3.0.2", {"start": v(21.3, -14.78) * mm, "end": v(21.9, -14.92) * mm});
            skPoint(sketch, "E66.3.0.3", {"position": v(15.84, -13.49) * mm});
            skPoint(sketch, "E66.3.0.4", {"position": v(22.76, -15.13) * mm});
            skPoint(sketch, "E66.3.0.5", {"position": v(14.97, -13.28) * mm});
            skPoint(sketch, "E66.3.0.6", {"position": v(23.9, -15.4) * mm});
            skPoint(sketch, "E66.3.0.7", {"position": v(16.98, -13.76) * mm});
            skPoint(sketch, "E66.3.0.8", {"position": v(20.44, -14.58) * mm});
            skPoint(sketch, "E66.3.0.9", {"position": v(18.7, -14.17) * mm});
            skPoint(sketch, "E66.3.0.10", {"position": v(15.25, -13.35) * mm});
            skLineSegment(sketch, "E66.3.0.11", {"start": v(17.84, -13.96) * mm, "end": v(18.43, -14.1) * mm});
            skLineSegment(sketch, "E66.3.0.12", {"start": v(20.44, -14.58) * mm, "end": v(21.03, -14.72) * mm});
            skPoint(sketch, "E66.3.0.13", {"position": v(18.28, -13.75) * mm});
            skPoint(sketch, "E66.3.0.14", {"position": v(21.75, -14.57) * mm});
            skPoint(sketch, "E66.3.0.15", {"position": v(21.9, -14.92) * mm});
            skPoint(sketch, "E66.3.0.16", {"position": v(14.38, -13.14) * mm});
            skLineSegment(sketch, "E66.3.0.17", {"start": v(22.17, -14.99) * mm, "end": v(22.61, -14.78) * mm});
            skLineSegment(sketch, "E66.3.0.18", {"start": v(19.57, -14.37) * mm, "end": v(20.16, -14.51) * mm});
            skPoint(sketch, "E66.3.0.19", {"position": v(16.28, -13.28) * mm});
            skPoint(sketch, "E66.3.0.20", {"position": v(19.74, -14.1) * mm});
            skPoint(sketch, "E66.3.0.21", {"position": v(22.17, -14.99) * mm});
            skPoint(sketch, "E66.3.0.22", {"position": v(18.01, -13.69) * mm});
            skPoint(sketch, "E66.3.0.23", {"position": v(17.15, -13.48) * mm});
            skPoint(sketch, "E66.3.0.24", {"position": v(21.47, -14.5) * mm});
            skLineSegment(sketch, "E66.3.0.25", {"start": v(16.98, -13.76) * mm, "end": v(17.57, -13.9) * mm});
            skPoint(sketch, "E66.3.0.26", {"position": v(20.6, -14.3) * mm});
            skPoint(sketch, "E66.3.0.27", {"position": v(16.55, -13.34) * mm});
            skPoint(sketch, "E66.3.0.28", {"position": v(20.01, -14.16) * mm});
            skPoint(sketch, "E66.3.0.29", {"position": v(16.7, -13.7) * mm});
            skPoint(sketch, "E66.3.0.30", {"position": v(20.16, -14.51) * mm});
            skLineSegment(sketch, "E66.3.0.31", {"start": v(21.9, -14.92) * mm, "end": v(22.34, -14.71) * mm});
            skPoint(sketch, "E66.3.0.32", {"position": v(23.62, -15.33) * mm});
            skLineSegment(sketch, "E66.3.0.33", {"start": v(22.17, -14.99) * mm, "end": v(22.76, -15.13) * mm});
            skPoint(sketch, "E66.3.0.34", {"position": v(18.43, -14.1) * mm});
            skPoint(sketch, "E66.3.0.35", {"position": v(16.11, -13.55) * mm});
            skPoint(sketch, "E66.3.0.36", {"position": v(19.57, -14.37) * mm});
            skLineSegment(sketch, "E66.3.0.37", {"start": v(16.11, -13.55) * mm, "end": v(16.7, -13.7) * mm});
            skLineSegment(sketch, "E66.3.0.38", {"start": v(18.7, -14.17) * mm, "end": v(19.3, -14.3) * mm});
            skPoint(sketch, "E66.3.0.39", {"position": v(23.03, -15.2) * mm});
            skLineSegment(sketch, "E66.3.0.40", {"start": v(15.25, -13.35) * mm, "end": v(15.84, -13.49) * mm});
            skLineSegment(sketch, "E66.3.0.41", {"start": v(23.03, -15.2) * mm, "end": v(23.62, -15.33) * mm});
            skPoint(sketch, "E66.3.0.42", {"position": v(19.15, -13.96) * mm});
            skPoint(sketch, "E66.3.0.43", {"position": v(17.57, -13.9) * mm});
            skPoint(sketch, "E66.3.0.44", {"position": v(17.42, -13.55) * mm});
            skPoint(sketch, "E66.3.0.45", {"position": v(20.88, -14.37) * mm});
            skPoint(sketch, "E66.3.0.46", {"position": v(17.84, -13.96) * mm});
            skPoint(sketch, "E66.3.0.47", {"position": v(21.03, -14.72) * mm});
            skPoint(sketch, "E66.3.0.48", {"position": v(21.3, -14.78) * mm});
            skPoint(sketch, "E66.3.0.49", {"position": v(15.69, -13.14) * mm});
            skPoint(sketch, "E66.3.0.50", {"position": v(14.82, -12.93) * mm});
            skPoint(sketch, "E66.3.0.51", {"position": v(15.42, -13.07) * mm});
            skLineSegment(sketch, "E66.3.0.52", {"start": v(20.16, -14.51) * mm, "end": v(20.6, -14.3) * mm});
            skPoint(sketch, "E66.3.0.53", {"position": v(24.07, -15.12) * mm});
            skLineSegment(sketch, "E66.3.0.54", {"start": v(16.11, -13.55) * mm, "end": v(16.55, -13.34) * mm});
            skLineSegment(sketch, "E66.3.0.55", {"start": v(16.7, -13.7) * mm, "end": v(17.15, -13.48) * mm});
            skLineSegment(sketch, "E66.3.0.56", {"start": v(15.25, -13.35) * mm, "end": v(15.69, -13.14) * mm});
            skLineSegment(sketch, "E66.3.0.57", {"start": v(20.44, -14.58) * mm, "end": v(20.88, -14.37) * mm});
            skLineSegment(sketch, "E66.3.0.58", {"start": v(18.43, -14.1) * mm, "end": v(18.88, -13.9) * mm});
            skLineSegment(sketch, "E66.3.0.59", {"start": v(14.97, -13.28) * mm, "end": v(15.42, -13.07) * mm});
            skLineSegment(sketch, "E66.3.0.60", {"start": v(17.57, -13.9) * mm, "end": v(18.01, -13.69) * mm});
            skLineSegment(sketch, "E66.3.0.61", {"start": v(18.7, -14.17) * mm, "end": v(19.15, -13.96) * mm});
            skLineSegment(sketch, "E66.3.0.62", {"start": v(21.03, -14.72) * mm, "end": v(21.47, -14.5) * mm});
            skLineSegment(sketch, "E66.3.0.63", {"start": v(17.84, -13.96) * mm, "end": v(18.28, -13.75) * mm});
            skLineSegment(sketch, "E66.3.0.64", {"start": v(16.98, -13.76) * mm, "end": v(17.42, -13.55) * mm});
            skLineSegment(sketch, "E66.3.0.65", {"start": v(19.57, -14.37) * mm, "end": v(20.01, -14.16) * mm});
            skLineSegment(sketch, "E66.3.0.66", {"start": v(15.84, -13.49) * mm, "end": v(16.28, -13.28) * mm});
            skLineSegment(sketch, "E66.3.0.67", {"start": v(21.3, -14.78) * mm, "end": v(21.75, -14.57) * mm});
            skLineSegment(sketch, "E66.3.0.68", {"start": v(19.3, -14.3) * mm, "end": v(19.74, -14.1) * mm});
            skPoint(sketch, "E66.3.0.69", {"position": v(24.34, -15.19) * mm});
            skLineSegment(sketch, "E66.3.0.70", {"start": v(14.38, -13.14) * mm, "end": v(14.97, -13.28) * mm});
            skPoint(sketch, "E66.3.0.71", {"position": v(22.34, -14.71) * mm});
            skPoint(sketch, "E66.3.0.72", {"position": v(22.61, -14.78) * mm});
            skLineSegment(sketch, "E66.3.0.73", {"start": v(22.76, -15.13) * mm, "end": v(23.2, -14.92) * mm});
            skPoint(sketch, "E66.3.0.74", {"position": v(23.2, -14.92) * mm});
            skPoint(sketch, "E66.3.0.75", {"position": v(23.48, -14.98) * mm});
            skLineSegment(sketch, "E66.3.0.76", {"start": v(23.03, -15.2) * mm, "end": v(23.48, -14.98) * mm});
            skLineSegment(sketch, "E66.3.0.77", {"start": v(23.62, -15.33) * mm, "end": v(24.07, -15.12) * mm});
            skLineSegment(sketch, "E66.3.0.78", {"start": v(23.9, -15.4) * mm, "end": v(24.34, -15.19) * mm});
            skLineSegment(sketch, "E66.3.0.79", {"start": v(23.9, -15.4) * mm, "end": v(24.49, -15.54) * mm});
            skLineSegment(sketch, "E66.3.0.80", {"start": v(24.49, -15.54) * mm, "end": v(24.93, -15.33) * mm});
            skLineSegment(sketch, "E66.3.0.81", {"start": v(24.76, -15.6) * mm, "end": v(25.2, -15.4) * mm});
            skLineSegment(sketch, "E66.3.0.82", {"start": v(24.76, -15.6) * mm, "end": v(25.35, -15.74) * mm});
            skLineSegment(sketch, "E66.3.0.83", {"start": v(25.35, -15.74) * mm, "end": v(25.8, -15.53) * mm});
            skPoint(sketch, "E66.3.0.84", {"position": v(25.35, -15.74) * mm});
            skPoint(sketch, "E66.3.0.85", {"position": v(24.76, -15.6) * mm});
            skPoint(sketch, "E66.3.0.86", {"position": v(24.49, -15.54) * mm});
            skPoint(sketch, "E66.3.0.87", {"position": v(24.93, -15.33) * mm});
            skPoint(sketch, "E66.3.0.88", {"position": v(25.2, -15.4) * mm});
            skPoint(sketch, "E66.3.0.89", {"position": v(25.8, -15.53) * mm});
            skPoint(sketch, "E66.3.0.90", {"position": v(26.66, -15.74) * mm});
            skPoint(sketch, "E66.3.0.91", {"position": v(27.36, -16.22) * mm});
            skLineSegment(sketch, "E66.3.0.92", {"start": v(25.63, -15.8) * mm, "end": v(26.07, -15.6) * mm});
            skLineSegment(sketch, "E66.3.0.93", {"start": v(28.22, -16.42) * mm, "end": v(28.82, -16.56) * mm});
            skLineSegment(sketch, "E66.3.0.94", {"start": v(27.08, -16.15) * mm, "end": v(27.53, -15.94) * mm});
            skLineSegment(sketch, "E66.3.0.95", {"start": v(27.36, -16.22) * mm, "end": v(27.95, -16.36) * mm});
            skPoint(sketch, "E66.3.0.96", {"position": v(29.09, -16.62) * mm});
            skLineSegment(sketch, "E66.3.0.97", {"start": v(27.95, -16.36) * mm, "end": v(28.4, -16.15) * mm});
            skPoint(sketch, "E66.3.0.98", {"position": v(26.94, -15.8) * mm});
            skPoint(sketch, "E66.3.0.99", {"position": v(27.53, -15.94) * mm});
            skPoint(sketch, "E66.3.0.100", {"position": v(27.08, -16.15) * mm});
            skPoint(sketch, "E66.3.0.101", {"position": v(28.82, -16.56) * mm});
            skLineSegment(sketch, "E66.3.0.102", {"start": v(28.22, -16.42) * mm, "end": v(28.67, -16.21) * mm});
            skLineSegment(sketch, "E66.3.0.103", {"start": v(29.09, -16.62) * mm, "end": v(29.68, -16.76) * mm});
            skLineSegment(sketch, "E66.3.0.104", {"start": v(26.22, -15.95) * mm, "end": v(26.66, -15.74) * mm});
            skLineSegment(sketch, "E66.3.0.105", {"start": v(29.09, -16.62) * mm, "end": v(29.53, -16.42) * mm});
            skLineSegment(sketch, "E66.3.0.106", {"start": v(28.82, -16.56) * mm, "end": v(29.26, -16.35) * mm});
            skLineSegment(sketch, "E66.3.0.107", {"start": v(26.5, -16.01) * mm, "end": v(26.94, -15.8) * mm});
            skLineSegment(sketch, "E66.3.0.108", {"start": v(27.36, -16.22) * mm, "end": v(27.8, -16) * mm});
            skPoint(sketch, "E66.3.0.109", {"position": v(26.07, -15.6) * mm});
            skPoint(sketch, "E66.3.0.110", {"position": v(27.8, -16) * mm});
            skPoint(sketch, "E66.3.0.111", {"position": v(27.95, -16.36) * mm});
            skPoint(sketch, "E66.3.0.112", {"position": v(28.22, -16.42) * mm});
            skLineSegment(sketch, "E66.3.0.113", {"start": v(26.5, -16.01) * mm, "end": v(27.08, -16.15) * mm});
            skPoint(sketch, "E66.3.0.114", {"position": v(26.5, -16.01) * mm});
            skPoint(sketch, "E66.3.0.115", {"position": v(26.22, -15.95) * mm});
            skLineSegment(sketch, "E66.3.0.116", {"start": v(25.63, -15.8) * mm, "end": v(26.22, -15.95) * mm});
            skPoint(sketch, "E66.3.0.117", {"position": v(25.63, -15.8) * mm});
            skPoint(sketch, "E66.3.0.118", {"position": v(28.4, -16.15) * mm});
            skPoint(sketch, "E66.3.0.119", {"position": v(28.67, -16.21) * mm});
            skPoint(sketch, "E66.3.0.120", {"position": v(29.26, -16.35) * mm});
            skPoint(sketch, "E66.3.0.121", {"position": v(29.53, -16.42) * mm});
            skPoint(sketch, "E66.3.0.122", {"position": v(29.68, -16.76) * mm});
            skPoint(sketch, "E66.3.0.123", {"position": v(30.12, -16.56) * mm});
            skPoint(sketch, "E66.4.0.0", {"position": v(18.15, -14.85) * mm});
            skPoint(sketch, "E66.4.0.1", {"position": v(17.73, -14.44) * mm});
            skLineSegment(sketch, "E66.4.0.2", {"start": v(20.16, -15.33) * mm, "end": v(20.75, -15.46) * mm});
            skPoint(sketch, "E66.4.0.3", {"position": v(14.7, -14.03) * mm});
            skPoint(sketch, "E66.4.0.4", {"position": v(21.61, -15.67) * mm});
            skPoint(sketch, "E66.4.0.5", {"position": v(13.83, -13.83) * mm});
            skPoint(sketch, "E66.4.0.6", {"position": v(22.75, -15.94) * mm});
            skPoint(sketch, "E66.4.0.7", {"position": v(15.83, -14.3) * mm});
            skPoint(sketch, "E66.4.0.8", {"position": v(19.3, -15.12) * mm});
            skPoint(sketch, "E66.4.0.9", {"position": v(17.56, -14.71) * mm});
            skPoint(sketch, "E66.4.0.10", {"position": v(14.1, -13.9) * mm});
            skLineSegment(sketch, "E66.4.0.11", {"start": v(16.7, -14.5) * mm, "end": v(17.29, -14.65) * mm});
            skLineSegment(sketch, "E66.4.0.12", {"start": v(19.3, -15.12) * mm, "end": v(19.88, -15.26) * mm});
            skPoint(sketch, "E66.4.0.13", {"position": v(17.14, -14.3) * mm});
            skPoint(sketch, "E66.4.0.14", {"position": v(20.6, -15.12) * mm});
            skPoint(sketch, "E66.4.0.15", {"position": v(20.75, -15.46) * mm});
            skPoint(sketch, "E66.4.0.16", {"position": v(13.24, -13.69) * mm});
            skLineSegment(sketch, "E66.4.0.17", {"start": v(21.02, -15.53) * mm, "end": v(21.46, -15.32) * mm});
            skLineSegment(sketch, "E66.4.0.18", {"start": v(18.43, -14.92) * mm, "end": v(19.02, -15.06) * mm});
            skPoint(sketch, "E66.4.0.19", {"position": v(15.13, -13.82) * mm});
            skPoint(sketch, "E66.4.0.20", {"position": v(18.6, -14.64) * mm});
            skPoint(sketch, "E66.4.0.21", {"position": v(21.02, -15.53) * mm});
            skPoint(sketch, "E66.4.0.22", {"position": v(16.86, -14.23) * mm});
            skPoint(sketch, "E66.4.0.23", {"position": v(16, -14.03) * mm});
            skPoint(sketch, "E66.4.0.24", {"position": v(20.32, -15.05) * mm});
            skLineSegment(sketch, "E66.4.0.25", {"start": v(15.83, -14.3) * mm, "end": v(16.42, -14.44) * mm});
            skPoint(sketch, "E66.4.0.26", {"position": v(19.46, -14.85) * mm});
            skPoint(sketch, "E66.4.0.27", {"position": v(15.4, -13.89) * mm});
            skPoint(sketch, "E66.4.0.28", {"position": v(18.87, -14.7) * mm});
            skPoint(sketch, "E66.4.0.29", {"position": v(15.56, -14.24) * mm});
            skPoint(sketch, "E66.4.0.30", {"position": v(19.02, -15.06) * mm});
            skLineSegment(sketch, "E66.4.0.31", {"start": v(20.75, -15.46) * mm, "end": v(21.19, -15.26) * mm});
            skPoint(sketch, "E66.4.0.32", {"position": v(22.48, -15.87) * mm});
            skLineSegment(sketch, "E66.4.0.33", {"start": v(21.02, -15.53) * mm, "end": v(21.61, -15.67) * mm});
            skPoint(sketch, "E66.4.0.34", {"position": v(17.29, -14.65) * mm});
            skPoint(sketch, "E66.4.0.35", {"position": v(14.97, -14.1) * mm});
            skPoint(sketch, "E66.4.0.36", {"position": v(18.43, -14.92) * mm});
            skLineSegment(sketch, "E66.4.0.37", {"start": v(14.97, -14.1) * mm, "end": v(15.56, -14.24) * mm});
            skLineSegment(sketch, "E66.4.0.38", {"start": v(17.56, -14.71) * mm, "end": v(18.15, -14.85) * mm});
            skPoint(sketch, "E66.4.0.39", {"position": v(21.89, -15.73) * mm});
            skLineSegment(sketch, "E66.4.0.40", {"start": v(14.1, -13.9) * mm, "end": v(14.7, -14.03) * mm});
            skLineSegment(sketch, "E66.4.0.41", {"start": v(21.89, -15.73) * mm, "end": v(22.48, -15.87) * mm});
            skPoint(sketch, "E66.4.0.42", {"position": v(18, -14.5) * mm});
            skPoint(sketch, "E66.4.0.43", {"position": v(16.42, -14.44) * mm});
            skPoint(sketch, "E66.4.0.44", {"position": v(16.27, -14.1) * mm});
            skPoint(sketch, "E66.4.0.45", {"position": v(19.73, -14.91) * mm});
            skPoint(sketch, "E66.4.0.46", {"position": v(16.7, -14.5) * mm});
            skPoint(sketch, "E66.4.0.47", {"position": v(19.88, -15.26) * mm});
            skPoint(sketch, "E66.4.0.48", {"position": v(20.16, -15.33) * mm});
            skPoint(sketch, "E66.4.0.49", {"position": v(14.54, -13.68) * mm});
            skPoint(sketch, "E66.4.0.50", {"position": v(13.68, -13.48) * mm});
            skPoint(sketch, "E66.4.0.51", {"position": v(14.27, -13.62) * mm});
            skPoint(sketch, "E66.4.0.53", {"position": v(22.92, -15.67) * mm});
            skLineSegment(sketch, "E66.4.0.54", {"start": v(14.97, -14.1) * mm, "end": v(15.4, -13.89) * mm});
            skLineSegment(sketch, "E66.4.0.55", {"start": v(15.56, -14.24) * mm, "end": v(16, -14.03) * mm});
            skLineSegment(sketch, "E66.4.0.56", {"start": v(14.1, -13.9) * mm, "end": v(14.54, -13.68) * mm});
            skLineSegment(sketch, "E66.4.0.59", {"start": v(13.83, -13.83) * mm, "end": v(14.27, -13.62) * mm});
            skLineSegment(sketch, "E66.4.0.60", {"start": v(16.42, -14.44) * mm, "end": v(16.86, -14.23) * mm});
            skLineSegment(sketch, "E66.4.0.62", {"start": v(19.88, -15.26) * mm, "end": v(20.32, -15.05) * mm});
            skLineSegment(sketch, "E66.4.0.63", {"start": v(16.7, -14.5) * mm, "end": v(17.14, -14.3) * mm});
            skLineSegment(sketch, "E66.4.0.64", {"start": v(15.83, -14.3) * mm, "end": v(16.27, -14.1) * mm});
            skLineSegment(sketch, "E66.4.0.66", {"start": v(14.7, -14.03) * mm, "end": v(15.13, -13.82) * mm});
            skLineSegment(sketch, "E66.4.0.67", {"start": v(20.16, -15.33) * mm, "end": v(20.6, -15.12) * mm});
            skPoint(sketch, "E66.4.0.69", {"position": v(23.2, -15.73) * mm});
            skLineSegment(sketch, "E66.4.0.70", {"start": v(13.24, -13.69) * mm, "end": v(13.83, -13.83) * mm});
            skPoint(sketch, "E66.4.0.71", {"position": v(21.19, -15.26) * mm});
            skPoint(sketch, "E66.4.0.72", {"position": v(21.46, -15.32) * mm});
            skLineSegment(sketch, "E66.4.0.73", {"start": v(21.61, -15.67) * mm, "end": v(22.05, -15.46) * mm});
            skPoint(sketch, "E66.4.0.74", {"position": v(22.05, -15.46) * mm});
            skPoint(sketch, "E66.4.0.75", {"position": v(22.33, -15.53) * mm});
            skLineSegment(sketch, "E66.4.0.76", {"start": v(21.89, -15.73) * mm, "end": v(22.33, -15.53) * mm});
            skLineSegment(sketch, "E66.4.0.77", {"start": v(22.48, -15.87) * mm, "end": v(22.92, -15.67) * mm});
            skLineSegment(sketch, "E66.4.0.78", {"start": v(22.75, -15.94) * mm, "end": v(23.2, -15.73) * mm});
            skLineSegment(sketch, "E66.4.0.79", {"start": v(22.75, -15.94) * mm, "end": v(23.34, -16.08) * mm});
            skLineSegment(sketch, "E66.4.0.80", {"start": v(23.34, -16.08) * mm, "end": v(23.78, -15.87) * mm});
            skLineSegment(sketch, "E66.4.0.81", {"start": v(23.62, -16.14) * mm, "end": v(24.06, -15.94) * mm});
            skLineSegment(sketch, "E66.4.0.82", {"start": v(23.62, -16.14) * mm, "end": v(24.2, -16.28) * mm});
            skLineSegment(sketch, "E66.4.0.83", {"start": v(24.2, -16.28) * mm, "end": v(24.65, -16.08) * mm});
            skPoint(sketch, "E66.4.0.84", {"position": v(24.2, -16.28) * mm});
            skPoint(sketch, "E66.4.0.85", {"position": v(23.62, -16.14) * mm});
            skPoint(sketch, "E66.4.0.86", {"position": v(23.34, -16.08) * mm});
            skPoint(sketch, "E66.4.0.87", {"position": v(23.78, -15.87) * mm});
            skPoint(sketch, "E66.4.0.88", {"position": v(24.06, -15.94) * mm});
            skPoint(sketch, "E66.4.0.89", {"position": v(24.65, -16.08) * mm});
            skPoint(sketch, "E66.4.0.90", {"position": v(25.51, -16.28) * mm});
            skPoint(sketch, "E66.4.0.91", {"position": v(26.21, -16.76) * mm});
            skLineSegment(sketch, "E66.4.0.92", {"start": v(24.48, -16.35) * mm, "end": v(24.92, -16.14) * mm});
            skLineSegment(sketch, "E66.4.0.93", {"start": v(27.08, -16.96) * mm, "end": v(27.67, -17.1) * mm});
            skLineSegment(sketch, "E66.4.0.94", {"start": v(25.94, -16.7) * mm, "end": v(26.38, -16.48) * mm});
            skLineSegment(sketch, "E66.4.0.95", {"start": v(26.21, -16.76) * mm, "end": v(26.8, -16.9) * mm});
            skPoint(sketch, "E66.4.0.96", {"position": v(27.94, -17.17) * mm});
            skLineSegment(sketch, "E66.4.0.97", {"start": v(26.8, -16.9) * mm, "end": v(27.24, -16.69) * mm});
            skPoint(sketch, "E66.4.0.98", {"position": v(25.79, -16.34) * mm});
            skPoint(sketch, "E66.4.0.99", {"position": v(26.38, -16.48) * mm});
            skPoint(sketch, "E66.4.0.100", {"position": v(25.94, -16.7) * mm});
            skPoint(sketch, "E66.4.0.101", {"position": v(27.67, -17.1) * mm});
            skLineSegment(sketch, "E66.4.0.102", {"start": v(27.08, -16.96) * mm, "end": v(27.52, -16.75) * mm});
            skLineSegment(sketch, "E66.4.0.103", {"start": v(27.94, -17.17) * mm, "end": v(28.53, -17.3) * mm});
            skLineSegment(sketch, "E66.4.0.104", {"start": v(25.07, -16.49) * mm, "end": v(25.51, -16.28) * mm});
            skLineSegment(sketch, "E66.4.0.105", {"start": v(27.94, -17.17) * mm, "end": v(28.38, -16.96) * mm});
            skLineSegment(sketch, "E66.4.0.106", {"start": v(27.67, -17.1) * mm, "end": v(28.1, -16.9) * mm});
            skLineSegment(sketch, "E66.4.0.107", {"start": v(25.35, -16.55) * mm, "end": v(25.79, -16.34) * mm});
            skLineSegment(sketch, "E66.4.0.108", {"start": v(26.21, -16.76) * mm, "end": v(26.65, -16.55) * mm});
            skPoint(sketch, "E66.4.0.109", {"position": v(24.92, -16.14) * mm});
            skPoint(sketch, "E66.4.0.110", {"position": v(26.65, -16.55) * mm});
            skPoint(sketch, "E66.4.0.111", {"position": v(26.8, -16.9) * mm});
            skPoint(sketch, "E66.4.0.112", {"position": v(27.08, -16.96) * mm});
            skLineSegment(sketch, "E66.4.0.113", {"start": v(25.35, -16.55) * mm, "end": v(25.94, -16.7) * mm});
            skPoint(sketch, "E66.4.0.114", {"position": v(25.35, -16.55) * mm});
            skPoint(sketch, "E66.4.0.115", {"position": v(25.07, -16.49) * mm});
            skLineSegment(sketch, "E66.4.0.116", {"start": v(24.48, -16.35) * mm, "end": v(25.07, -16.49) * mm});
            skPoint(sketch, "E66.4.0.117", {"position": v(24.48, -16.35) * mm});
            skPoint(sketch, "E66.4.0.118", {"position": v(27.24, -16.69) * mm});
            skPoint(sketch, "E66.4.0.119", {"position": v(27.52, -16.75) * mm});
            skPoint(sketch, "E66.4.0.120", {"position": v(28.1, -16.9) * mm});
            skPoint(sketch, "E66.4.0.121", {"position": v(28.38, -16.96) * mm});
            skPoint(sketch, "E66.4.0.122", {"position": v(28.53, -17.3) * mm});
            skPoint(sketch, "E66.4.0.123", {"position": v(28.97, -17.1) * mm});
            skLineSegment(sketch, "E66.direction1", {"start": v(17.83, -11.51) * mm, "end": v(17.12, -11.85) * mm, "construction": true});
            skLineSegment(sketch, "E67", {"start": v(17.12, -11.85) * mm, "end": v(20.3, -12.6) * mm});
            skLineSegment(sketch, "E68", {"start": v(32.42, -15.47) * mm, "end": v(31.83, -15.33) * mm});
            skLineSegment(sketch, "E69.trimOffspring", {"start": v(30.96, -15.12) * mm, "end": v(31.55, -15.26) * mm});
            skLineSegment(sketch, "E70.trimOffspring", {"start": v(30.1, -14.92) * mm, "end": v(30.69, -15.06) * mm});
            skLineSegment(sketch, "E71.trimOffspring", {"start": v(29.23, -14.71) * mm, "end": v(29.82, -14.85) * mm});
            skLineSegment(sketch, "E72.trimOffspring", {"start": v(28.37, -14.5) * mm, "end": v(28.96, -14.65) * mm});
            skLineSegment(sketch, "E73.trimOffspring", {"start": v(27.5, -14.3) * mm, "end": v(28.1, -14.44) * mm});
            skLineSegment(sketch, "E74.trimOffspring", {"start": v(26.64, -14.1) * mm, "end": v(27.23, -14.24) * mm});
            skLineSegment(sketch, "E75.trimOffspring", {"start": v(25.77, -13.9) * mm, "end": v(26.36, -14.04) * mm});
            skLineSegment(sketch, "E76.trimOffspring", {"start": v(24.9, -13.7) * mm, "end": v(25.5, -13.83) * mm});
            skLineSegment(sketch, "E77", {"start": v(26.35, -14.85) * mm, "end": v(26.94, -14.99) * mm});
            skLineSegment(sketch, "E78", {"start": v(27.22, -15.05) * mm, "end": v(27.8, -15.2) * mm});
            skLineSegment(sketch, "E79", {"start": v(28.08, -15.26) * mm, "end": v(28.67, -15.4) * mm});
            skLineSegment(sketch, "E80", {"start": v(28.95, -15.46) * mm, "end": v(29.54, -15.6) * mm});
            skLineSegment(sketch, "E81", {"start": v(29.81, -15.67) * mm, "end": v(30.4, -15.8) * mm});
            skLineSegment(sketch, "E82", {"start": v(30.68, -15.87) * mm, "end": v(31.27, -16.01) * mm});
            skLineSegment(sketch, "E83", {"start": v(30.12, -16.56) * mm, "end": v(29.53, -16.42) * mm});
            skLineSegment(sketch, "E84", {"start": v(28.97, -17.1) * mm, "end": v(28.38, -16.96) * mm});
            skLineSegment(sketch, "E85", {"start": v(28.1, -16.9) * mm, "end": v(27.52, -16.75) * mm});
            skLineSegment(sketch, "E86", {"start": v(27.24, -16.69) * mm, "end": v(26.65, -16.55) * mm});
            skLineSegment(sketch, "E87", {"start": v(25.79, -16.34) * mm, "end": v(26.38, -16.48) * mm});
            skLineSegment(sketch, "E88", {"start": v(25.51, -16.28) * mm, "end": v(24.92, -16.14) * mm});
            skLineSegment(sketch, "E89", {"start": v(24.65, -16.08) * mm, "end": v(24.06, -15.94) * mm});
            skLineSegment(sketch, "E90", {"start": v(23.2, -15.73) * mm, "end": v(23.78, -15.87) * mm});
            skLineSegment(sketch, "E91", {"start": v(20.32, -15.05) * mm, "end": v(17.14, -14.3) * mm});
            skLineSegment(sketch, "E92", {"start": v(17.29, -14.65) * mm, "end": v(18.43, -14.92) * mm});
            skLineSegment(sketch, "E93.trimOffspring", {"start": v(19.02, -15.06) * mm, "end": v(19.3, -15.12) * mm});
            skLineSegment(sketch, "E94", {"start": v(12.5, -14.03) * mm, "end": v(16.4, -14.96) * mm});
            skLineSegment(sketch, "E95.trimOffspring", {"start": v(24.04, -13.49) * mm, "end": v(24.63, -13.63) * mm});
            skLineSegment(sketch, "E96.trimOffspring", {"start": v(23.18, -13.28) * mm, "end": v(23.77, -13.42) * mm});
            skLineSegment(sketch, "E97.trimOffspring", {"start": v(22.31, -13.08) * mm, "end": v(22.9, -13.22) * mm});
            skLineSegment(sketch, "E98.trimOffspring", {"start": v(21.45, -12.87) * mm, "end": v(22.04, -13.01) * mm});
            skLineSegment(sketch, "E99.trimOffspring", {"start": v(20.58, -12.67) * mm, "end": v(21.17, -12.8) * mm});
            skLineSegment(sketch, "E100", {"start": v(21.16, -13.62) * mm, "end": v(21.75, -13.76) * mm});
            skLineSegment(sketch, "E101", {"start": v(22.03, -13.82) * mm, "end": v(22.62, -13.96) * mm});
            skLineSegment(sketch, "E102", {"start": v(20.6, -15.12) * mm, "end": v(21.19, -15.26) * mm});
            skLineSegment(sketch, "E103", {"start": v(21.46, -15.32) * mm, "end": v(22.05, -15.46) * mm});
            skLineSegment(sketch, "E104", {"start": v(22.33, -15.53) * mm, "end": v(22.92, -15.67) * mm});
            skLineSegment(sketch, "E105", {"start": v(23.48, -14.98) * mm, "end": v(24.07, -15.12) * mm});
            skLineSegment(sketch, "E106", {"start": v(24.34, -15.19) * mm, "end": v(24.93, -15.33) * mm});
            skLineSegment(sketch, "E107", {"start": v(25.2, -15.4) * mm, "end": v(25.8, -15.53) * mm});
            skLineSegment(sketch, "E108", {"start": v(26.07, -15.6) * mm, "end": v(26.66, -15.74) * mm});
            skLineSegment(sketch, "E109", {"start": v(26.94, -15.8) * mm, "end": v(27.53, -15.94) * mm});
            skLineSegment(sketch, "E110", {"start": v(27.8, -16) * mm, "end": v(28.4, -16.15) * mm});
            skLineSegment(sketch, "E111", {"start": v(28.67, -16.21) * mm, "end": v(29.26, -16.35) * mm});
            skLineSegment(sketch, "E112", {"start": v(26.08, -14.78) * mm, "end": v(25.49, -14.64) * mm});
            skLineSegment(sketch, "E113", {"start": v(25.21, -14.58) * mm, "end": v(24.62, -14.44) * mm});
            skLineSegment(sketch, "E114", {"start": v(24.35, -14.37) * mm, "end": v(23.76, -14.23) * mm});
            skLineSegment(sketch, "E115", {"start": v(23.48, -14.17) * mm, "end": v(22.9, -14.03) * mm});
            skLineSegment(sketch, "E116", {"start": v(20.89, -13.55) * mm, "end": v(20.3, -13.41) * mm});
            skLineSegment(sketch, "E117", {"start": v(20.02, -13.35) * mm, "end": v(19.43, -13.21) * mm});
            skLineSegment(sketch, "E118", {"start": v(19.74, -14.1) * mm, "end": v(19.15, -13.96) * mm});
            skLineSegment(sketch, "E119", {"start": v(20.6, -14.3) * mm, "end": v(20.01, -14.16) * mm});
            skLineSegment(sketch, "E120", {"start": v(21.47, -14.5) * mm, "end": v(20.88, -14.37) * mm});
            skLineSegment(sketch, "E121", {"start": v(22.34, -14.71) * mm, "end": v(21.75, -14.57) * mm});
            skLineSegment(sketch, "E122", {"start": v(23.2, -14.92) * mm, "end": v(22.61, -14.78) * mm});
            skLineSegment(sketch, "E123", {"start": v(16.56, -12.53) * mm, "end": v(15.97, -12.4) * mm});
            skLineSegment(sketch, "E124", {"start": v(16.84, -12.6) * mm, "end": v(17.43, -12.74) * mm});
            skLineSegment(sketch, "E125", {"start": v(17.7, -12.8) * mm, "end": v(18.3, -12.94) * mm});
            skLineSegment(sketch, "E126", {"start": v(18.57, -13) * mm, "end": v(19.16, -13.15) * mm});
            skLineSegment(sketch, "E127", {"start": v(18.28, -13.75) * mm, "end": v(18.88, -13.9) * mm});
            skLineSegment(sketch, "E128", {"start": v(18.01, -13.69) * mm, "end": v(17.42, -13.55) * mm});
            skLineSegment(sketch, "E129", {"start": v(17.15, -13.48) * mm, "end": v(16.55, -13.34) * mm});
            skLineSegment(sketch, "E130", {"start": v(16.28, -13.28) * mm, "end": v(15.69, -13.14) * mm});
            skLineSegment(sketch, "E131", {"start": v(15.42, -13.07) * mm, "end": v(14.82, -12.93) * mm});
            skLineSegment(sketch, "E132", {"start": v(16, -14.03) * mm, "end": v(15.4, -13.89) * mm});
            skLineSegment(sketch, "E133", {"start": v(16.86, -14.23) * mm, "end": v(16.27, -14.1) * mm});
            skLineSegment(sketch, "E134", {"start": v(15.13, -13.82) * mm, "end": v(14.54, -13.68) * mm});
            skLineSegment(sketch, "E135", {"start": v(14.27, -13.62) * mm, "end": v(13.68, -13.48) * mm});
            skLineSegment(sketch, "E136", {"start": v(13.62, -16.56) * mm, "end": v(14.26, -16.25) * mm});
            skPoint(sketch, "E137.endSnap0", {"position": v(20.16, -15.85) * mm});
            skLineSegment(sketch, "E138", {"start": v(19.92, -15.96) * mm, "end": v(17.64, -17.04) * mm});
            skLineSegment(sketch, "E139", {"start": v(14.37, -16.2) * mm, "end": v(17.53, -17.1) * mm, "construction": true});
            skLineSegment(sketch, "E140", {"start": v(15.95, -16.65) * mm, "end": v(15.2, -17) * mm, "construction": true});
            skLineSegment(sketch, "E141", {"start": v(14.49, -16.15) * mm, "end": v(17.64, -17.04) * mm});
            skLineSegment(sketch, "E142", {"start": v(14.26, -16.25) * mm, "end": v(15.71, -16.67) * mm});
            skLineSegment(sketch, "E143", {"start": v(15.71, -16.67) * mm, "end": v(15.08, -16.97) * mm});
            skLineSegment(sketch, "E144", {"start": v(15.32, -17.04) * mm, "end": v(15.96, -16.74) * mm});
            skLineSegment(sketch, "E145", {"start": v(15.96, -16.74) * mm, "end": v(17.41, -17.15) * mm});
            skLineSegment(sketch, "E146", {"start": v(16.56, -15.17) * mm, "end": v(19.92, -15.96) * mm});
            skLineSegment(sketch, "E147.trimOffspring", {"start": v(17.41, -17.15) * mm, "end": v(16.78, -17.45) * mm});
            skLineSegment(sketch, "E148.trimOffspring", {"start": v(15.32, -17.04) * mm, "end": v(16.78, -17.45) * mm});
            skLineSegment(sketch, "E149.trimOffspring", {"start": v(14.49, -16.15) * mm, "end": v(16.56, -15.17) * mm});
            skLineSegment(sketch, "E150.0", {"start": v(37.66, -2.84) * mm, "end": v(21.6, 0.96) * mm});
            skLineSegment(sketch, "E150.1", {"start": v(35.03, -13.97) * mm, "end": v(37.66, -2.84) * mm});
            skLineSegment(sketch, "E150.2", {"start": v(18.96, -10.16) * mm, "end": v(35.03, -13.97) * mm});
            skLineSegment(sketch, "E150.3", {"start": v(21.6, 0.96) * mm, "end": v(18.96, -10.16) * mm});
            skLineSegment(sketch, "E151", {"start": v(16.4, -14.96) * mm, "end": v(12.9, -16.62) * mm});
            skLineSegment(sketch, "E152", {"start": v(12.9, -16.62) * mm, "end": v(16.8, -17.72) * mm});
            skLineSegment(sketch, "E153", {"start": v(16.8, -17.72) * mm, "end": v(20.56, -15.94) * mm});
            skLineSegment(sketch, "E154.trimOffspring", {"start": v(20.56, -15.94) * mm, "end": v(27.82, -17.66) * mm});
            skPoint(sketch, "E137.end.orphan", {"position": v(20.16, -15.85) * mm});
            skLineSegment(sketch, "E155.trimOffspring", {"start": v(13.24, -13.69) * mm, "end": v(12.5, -14.03) * mm});
            skLineSegment(sketch, "E156.trimOffspring", {"start": v(14.38, -13.14) * mm, "end": v(13.68, -13.48) * mm});
            skLineSegment(sketch, "E157.trimOffspring", {"start": v(15.53, -12.6) * mm, "end": v(14.82, -12.93) * mm});
            skLineSegment(sketch, "E158", {"start": v(28.53, -17.3) * mm, "end": v(28.56, -17.31) * mm});
            skLineSegment(sketch, "E159", {"start": v(28.97, -17.1) * mm, "end": v(29, -17.1) * mm});
            skLineSegment(sketch, "E160", {"start": v(29.68, -16.76) * mm, "end": v(29.7, -16.77) * mm});
            skLineSegment(sketch, "E161.trimOffspring", {"start": v(29, -17.1) * mm, "end": v(29.7, -16.77) * mm});
            skLineSegment(sketch, "E162", {"start": v(30.12, -16.56) * mm, "end": v(30.15, -16.56) * mm});
            skLineSegment(sketch, "E163", {"start": v(30.83, -16.22) * mm, "end": v(30.85, -16.23) * mm});
            skLineSegment(sketch, "E164", {"start": v(31.27, -16.01) * mm, "end": v(31.3, -16.02) * mm});
            skLineSegment(sketch, "E165.trimOffspring", {"start": v(30.15, -16.56) * mm, "end": v(30.85, -16.23) * mm});
            skLineSegment(sketch, "E166.trimOffspring", {"start": v(31.3, -16.02) * mm, "end": v(32, -15.68) * mm});
            skLineSegment(sketch, "E167", {"start": v(31.98, -15.68) * mm, "end": v(32, -15.68) * mm});
            skLineSegment(sketch, "E168", {"start": v(32.42, -15.47) * mm, "end": v(32.44, -15.47) * mm});
            skLineSegment(sketch, "E169.trimOffspring", {"start": v(32.44, -15.47) * mm, "end": v(33.15, -15.14) * mm});
            skLineSegment(sketch, "E170.trimOffspring", {"start": v(33.57, -14.93) * mm, "end": v(33.6, -14.93) * mm});
            skLineSegment(sketch, "E171.trimOffspring", {"start": v(32.7, -14.72) * mm, "end": v(32.97, -14.79) * mm});
            skLineSegment(sketch, "E172.trimOffspring", {"start": v(31.84, -14.52) * mm, "end": v(32.1, -14.58) * mm});
            skLineSegment(sketch, "E173.trimOffspring", {"start": v(30.97, -14.31) * mm, "end": v(31.24, -14.38) * mm});
            skLineSegment(sketch, "E174.trimOffspring", {"start": v(30.1, -14.1) * mm, "end": v(30.38, -14.17) * mm});
            skLineSegment(sketch, "E175.trimOffspring", {"start": v(29.24, -13.9) * mm, "end": v(29.51, -13.97) * mm});
            skLineSegment(sketch, "E176.trimOffspring", {"start": v(28.37, -13.7) * mm, "end": v(28.65, -13.76) * mm});
            skLineSegment(sketch, "E177.trimOffspring", {"start": v(27.5, -13.5) * mm, "end": v(27.78, -13.56) * mm});
            skLineSegment(sketch, "E178.trimOffspring", {"start": v(26.64, -13.29) * mm, "end": v(26.92, -13.35) * mm});
            skLineSegment(sketch, "E179.trimOffspring", {"start": v(25.78, -13.08) * mm, "end": v(26.05, -13.15) * mm});
            skLineSegment(sketch, "E180.trimOffspring", {"start": v(24.91, -12.88) * mm, "end": v(25.19, -12.94) * mm});
            skLineSegment(sketch, "E181.trimOffspring", {"start": v(24.05, -12.67) * mm, "end": v(24.32, -12.74) * mm});
            skLineSegment(sketch, "E182.trimOffspring", {"start": v(23.18, -12.47) * mm, "end": v(23.46, -12.53) * mm});
            skLineSegment(sketch, "E183.trimOffspring", {"start": v(22.32, -12.26) * mm, "end": v(22.6, -12.33) * mm});
            skLineSegment(sketch, "E184.trimOffspring", {"start": v(21.45, -12.06) * mm, "end": v(21.73, -12.12) * mm});
            skLineSegment(sketch, "E185.trimOffspring", {"start": v(20.59, -11.85) * mm, "end": v(20.86, -11.92) * mm});
            skLineSegment(sketch, "E186.trimOffspring", {"start": v(19.72, -11.65) * mm, "end": v(20, -11.71) * mm});
            skLineSegment(sketch, "E187.trimOffspring", {"start": v(16.68, -12.06) * mm, "end": v(15.97, -12.4) * mm});
            skSolve(sketch);
        }
        {
            var Q0;
            Q0=makeQuery(id+"F4.imprint","IMPRINT",FACE,{"disambiguationData":[TD([[makeQuery(id+"F4.imprint","IMPRINT",EDGE,{"derivedFrom":sQuery(id+"F4.wireOp",EDGE,"E34")}),1.0]])]});
            var Q1;
            Q1=makeQuery(id+"F4.imprint","IMPRINT",FACE,{"disambiguationData":[TD([[makeQuery(id+"F4.imprint","IMPRINT",EDGE,{"derivedFrom":sQuery(id+"F4.wireOp",EDGE,"E33")}),1.0]])]});
            var Q2;
            Q2=makeQuery(id+"F4.imprint","IMPRINT",FACE,{"disambiguationData":[TD([[makeQuery(id+"F4.imprint","IMPRINT",EDGE,{"derivedFrom":sQuery(id+"F4.wireOp",EDGE,"E138")}),-1.0]])]});
            var Q3;
            Q3=makeQuery(id+"F4.imprint","IMPRINT",FACE,{"disambiguationData":[TD([[makeQuery(id+"F4.imprint","IMPRINT",EDGE,{"derivedFrom":sQuery(id+"F4.wireOp",EDGE,"E40.2")}),1.0]])]});
            var Q4;
            Q4=makeQuery(id+"F4.imprint","IMPRINT",FACE,{"disambiguationData":[TD([[makeQuery(id+"F4.imprint","IMPRINT",EDGE,{"derivedFrom":sQuery(id+"F4.wireOp",EDGE,"E144")}),-1.0]])]});
            var Q5;
            Q5=makeQuery(id+"F4.imprint","IMPRINT",FACE,{"disambiguationData":[TD([[makeQuery(id+"F4.imprint","IMPRINT",EDGE,{"derivedFrom":sQuery(id+"F4.wireOp",EDGE,"E66.4.0.93")}),1.0]])]});
            var Q6;
            Q6=makeQuery(id+"F4.imprint","IMPRINT",FACE,{"disambiguationData":[TD([[makeQuery(id+"F4.imprint","IMPRINT",EDGE,{"derivedFrom":sQuery(id+"F4.wireOp",EDGE,"E66.4.0.95")}),1.0]])]});
            var Q7;
            Q7=makeQuery(id+"F4.imprint","IMPRINT",FACE,{"disambiguationData":[TD([[makeQuery(id+"F4.imprint","IMPRINT",EDGE,{"derivedFrom":sQuery(id+"F4.wireOp",EDGE,"E66.4.0.94")}),1.0]])]});
            var Q8;
            Q8=makeQuery(id+"F4.imprint","IMPRINT",FACE,{"disambiguationData":[TD([[makeQuery(id+"F4.imprint","IMPRINT",EDGE,{"derivedFrom":sQuery(id+"F4.wireOp",EDGE,"E66.4.0.92")}),-1.0]])]});
            var Q9;
            Q9=makeQuery(id+"F4.imprint","IMPRINT",FACE,{"disambiguationData":[TD([[makeQuery(id+"F4.imprint","IMPRINT",EDGE,{"derivedFrom":sQuery(id+"F4.wireOp",EDGE,"E66.4.0.81")}),-1.0]])]});
            var Q10;
            Q10=makeQuery(id+"F4.imprint","IMPRINT",FACE,{"disambiguationData":[TD([[makeQuery(id+"F4.imprint","IMPRINT",EDGE,{"derivedFrom":sQuery(id+"F4.wireOp",EDGE,"E66.4.0.78")}),-1.0]])]});
            var Q11;
            Q11=makeQuery(id+"F4.imprint","IMPRINT",FACE,{"disambiguationData":[TD([[makeQuery(id+"F4.imprint","IMPRINT",EDGE,{"derivedFrom":sQuery(id+"F4.wireOp",EDGE,"E66.4.0.41")}),1.0]])]});
            var Q12;
            Q12=makeQuery(id+"F4.imprint","IMPRINT",FACE,{"disambiguationData":[TD([[makeQuery(id+"F4.imprint","IMPRINT",EDGE,{"derivedFrom":sQuery(id+"F4.wireOp",EDGE,"E66.4.0.17")}),-1.0]])]});
            var Q13;
            Q13=makeQuery(id+"F4.imprint","IMPRINT",FACE,{"disambiguationData":[TD([[makeQuery(id+"F4.imprint","IMPRINT",EDGE,{"derivedFrom":sQuery(id+"F4.wireOp",EDGE,"E66.4.0.2")}),1.0]])]});
            var Q14;
            {var subQ1=sQuery(id+"F4.wireOp",EDGE,"E66.4.0.11");Q14=makeQuery(id+"F4.imprint","IMPRINT",FACE,{"disambiguationData":[TD([[makeQuery(id+"F4.imprint","IMPRINT",EDGE,{"derivedFrom":subQ1}),1.0]])]});}
            var Q15;
            Q15=makeQuery(id+"F4.imprint","IMPRINT",FACE,{"disambiguationData":[TD([[makeQuery(id+"F4.imprint","IMPRINT",EDGE,{"derivedFrom":sQuery(id+"F4.wireOp",EDGE,"E66.3.0.18")}),1.0]])]});
            var Q16;
            Q16=makeQuery(id+"F4.imprint","IMPRINT",FACE,{"disambiguationData":[TD([[makeQuery(id+"F4.imprint","IMPRINT",EDGE,{"derivedFrom":sQuery(id+"F4.wireOp",EDGE,"E66.3.0.38")}),1.0]])]});
            var Q17;
            Q17=makeQuery(id+"F4.imprint","IMPRINT",FACE,{"disambiguationData":[TD([[makeQuery(id+"F4.imprint","IMPRINT",EDGE,{"derivedFrom":sQuery(id+"F4.wireOp",EDGE,"E66.3.0.11")}),1.0]])]});
            var Q18;
            Q18=makeQuery(id+"F4.imprint","IMPRINT",FACE,{"disambiguationData":[TD([[makeQuery(id+"F4.imprint","IMPRINT",EDGE,{"derivedFrom":sQuery(id+"F4.wireOp",EDGE,"E66.3.0.25")}),1.0]])]});
            var Q19;
            Q19=makeQuery(id+"F4.imprint","IMPRINT",FACE,{"disambiguationData":[TD([[makeQuery(id+"F4.imprint","IMPRINT",EDGE,{"derivedFrom":sQuery(id+"F4.wireOp",EDGE,"E66.3.0.12")}),1.0]])]});
            var Q20;
            Q20=makeQuery(id+"F4.imprint","IMPRINT",FACE,{"disambiguationData":[TD([[makeQuery(id+"F4.imprint","IMPRINT",EDGE,{"derivedFrom":sQuery(id+"F4.wireOp",EDGE,"E66.3.0.2")}),1.0]])]});
            var Q21;
            Q21=makeQuery(id+"F4.imprint","IMPRINT",FACE,{"disambiguationData":[TD([[makeQuery(id+"F4.imprint","IMPRINT",EDGE,{"derivedFrom":sQuery(id+"F4.wireOp",EDGE,"E66.3.0.17")}),-1.0]])]});
            var Q22;
            Q22=makeQuery(id+"F4.imprint","IMPRINT",FACE,{"disambiguationData":[TD([[makeQuery(id+"F4.imprint","IMPRINT",EDGE,{"derivedFrom":sQuery(id+"F4.wireOp",EDGE,"E66.3.0.41")}),1.0]])]});
            var Q23;
            Q23=makeQuery(id+"F4.imprint","IMPRINT",FACE,{"disambiguationData":[TD([[makeQuery(id+"F4.imprint","IMPRINT",EDGE,{"derivedFrom":sQuery(id+"F4.wireOp",EDGE,"E66.3.0.78")}),-1.0]])]});
            var Q24;
            Q24=makeQuery(id+"F4.imprint","IMPRINT",FACE,{"disambiguationData":[TD([[makeQuery(id+"F4.imprint","IMPRINT",EDGE,{"derivedFrom":sQuery(id+"F4.wireOp",EDGE,"E66.3.0.81")}),-1.0]])]});
            var Q25;
            Q25=makeQuery(id+"F4.imprint","IMPRINT",FACE,{"disambiguationData":[TD([[makeQuery(id+"F4.imprint","IMPRINT",EDGE,{"derivedFrom":sQuery(id+"F4.wireOp",EDGE,"E66.3.0.92")}),-1.0]])]});
            var Q26;
            Q26=makeQuery(id+"F4.imprint","IMPRINT",FACE,{"disambiguationData":[TD([[makeQuery(id+"F4.imprint","IMPRINT",EDGE,{"derivedFrom":sQuery(id+"F4.wireOp",EDGE,"E66.3.0.94")}),1.0]])]});
            var Q27;
            Q27=makeQuery(id+"F4.imprint","IMPRINT",FACE,{"disambiguationData":[TD([[makeQuery(id+"F4.imprint","IMPRINT",EDGE,{"derivedFrom":sQuery(id+"F4.wireOp",EDGE,"E66.3.0.95")}),1.0]])]});
            var Q28;
            Q28=makeQuery(id+"F4.imprint","IMPRINT",FACE,{"disambiguationData":[TD([[makeQuery(id+"F4.imprint","IMPRINT",EDGE,{"derivedFrom":sQuery(id+"F4.wireOp",EDGE,"E66.3.0.93")}),1.0]])]});
            var Q29;
            Q29=makeQuery(id+"F4.imprint","IMPRINT",FACE,{"disambiguationData":[TD([[makeQuery(id+"F4.imprint","IMPRINT",EDGE,{"derivedFrom":sQuery(id+"F4.wireOp",EDGE,"E66.2.0.93")}),1.0]])]});
            var Q30;
            Q30=makeQuery(id+"F4.imprint","IMPRINT",FACE,{"disambiguationData":[TD([[makeQuery(id+"F4.imprint","IMPRINT",EDGE,{"derivedFrom":sQuery(id+"F4.wireOp",EDGE,"E66.2.0.95")}),1.0]])]});
            var Q31;
            Q31=makeQuery(id+"F4.imprint","IMPRINT",FACE,{"disambiguationData":[TD([[makeQuery(id+"F4.imprint","IMPRINT",EDGE,{"derivedFrom":sQuery(id+"F4.wireOp",EDGE,"E66.2.0.94")}),1.0]])]});
            var Q32;
            Q32=makeQuery(id+"F4.imprint","IMPRINT",FACE,{"disambiguationData":[TD([[makeQuery(id+"F4.imprint","IMPRINT",EDGE,{"derivedFrom":sQuery(id+"F4.wireOp",EDGE,"E66.2.0.92")}),-1.0]])]});
            var Q33;
            Q33=makeQuery(id+"F4.imprint","IMPRINT",FACE,{"disambiguationData":[TD([[makeQuery(id+"F4.imprint","IMPRINT",EDGE,{"derivedFrom":sQuery(id+"F4.wireOp",EDGE,"E66.2.0.81")}),-1.0]])]});
            var Q34;
            Q34=makeQuery(id+"F4.imprint","IMPRINT",FACE,{"disambiguationData":[TD([[makeQuery(id+"F4.imprint","IMPRINT",EDGE,{"derivedFrom":sQuery(id+"F4.wireOp",EDGE,"E66.2.0.78")}),-1.0]])]});
            var Q35;
            Q35=makeQuery(id+"F4.imprint","IMPRINT",FACE,{"disambiguationData":[TD([[makeQuery(id+"F4.imprint","IMPRINT",EDGE,{"derivedFrom":sQuery(id+"F4.wireOp",EDGE,"E66.2.0.41")}),1.0]])]});
            var Q36;
            Q36=makeQuery(id+"F4.imprint","IMPRINT",FACE,{"disambiguationData":[TD([[makeQuery(id+"F4.imprint","IMPRINT",EDGE,{"derivedFrom":sQuery(id+"F4.wireOp",EDGE,"E66.2.0.17")}),-1.0]])]});
            var Q37;
            Q37=makeQuery(id+"F4.imprint","IMPRINT",FACE,{"disambiguationData":[TD([[makeQuery(id+"F4.imprint","IMPRINT",EDGE,{"derivedFrom":sQuery(id+"F4.wireOp",EDGE,"E66.2.0.2")}),1.0]])]});
            var Q38;
            Q38=makeQuery(id+"F4.imprint","IMPRINT",FACE,{"disambiguationData":[TD([[makeQuery(id+"F4.imprint","IMPRINT",EDGE,{"derivedFrom":sQuery(id+"F4.wireOp",EDGE,"E66.2.0.12")}),1.0]])]});
            var Q39;
            Q39=makeQuery(id+"F4.imprint","IMPRINT",FACE,{"disambiguationData":[TD([[makeQuery(id+"F4.imprint","IMPRINT",EDGE,{"derivedFrom":sQuery(id+"F4.wireOp",EDGE,"E66.2.0.18")}),1.0]])]});
            var Q40;
            Q40=makeQuery(id+"F4.imprint","IMPRINT",FACE,{"disambiguationData":[TD([[makeQuery(id+"F4.imprint","IMPRINT",EDGE,{"derivedFrom":sQuery(id+"F4.wireOp",EDGE,"E66.2.0.38")}),1.0]])]});
            var Q41;
            Q41=makeQuery(id+"F4.imprint","IMPRINT",FACE,{"disambiguationData":[TD([[makeQuery(id+"F4.imprint","IMPRINT",EDGE,{"derivedFrom":sQuery(id+"F4.wireOp",EDGE,"E66.2.0.11")}),1.0]])]});
            var Q42;
            Q42=makeQuery(id+"F4.imprint","IMPRINT",FACE,{"disambiguationData":[TD([[makeQuery(id+"F4.imprint","IMPRINT",EDGE,{"derivedFrom":sQuery(id+"F4.wireOp",EDGE,"E66.2.0.25")}),1.0]])]});
            var Q43;
            Q43=makeQuery(id+"F4.imprint","IMPRINT",FACE,{"disambiguationData":[TD([[makeQuery(id+"F4.imprint","IMPRINT",EDGE,{"derivedFrom":sQuery(id+"F4.wireOp",EDGE,"E66.2.0.37")}),1.0]])]});
            var Q44;
            Q44=makeQuery(id+"F4.imprint","IMPRINT",FACE,{"disambiguationData":[TD([[makeQuery(id+"F4.imprint","IMPRINT",EDGE,{"derivedFrom":sQuery(id+"F4.wireOp",EDGE,"E66.1.0.40")}),1.0]])]});
            var Q45;
            Q45=makeQuery(id+"F4.imprint","IMPRINT",FACE,{"disambiguationData":[TD([[makeQuery(id+"F4.imprint","IMPRINT",EDGE,{"derivedFrom":sQuery(id+"F4.wireOp",EDGE,"E66.1.0.37")}),1.0]])]});
            var Q46;
            Q46=makeQuery(id+"F4.imprint","IMPRINT",FACE,{"disambiguationData":[TD([[makeQuery(id+"F4.imprint","IMPRINT",EDGE,{"derivedFrom":sQuery(id+"F4.wireOp",EDGE,"E66.1.0.25")}),1.0]])]});
            var Q47;
            Q47=makeQuery(id+"F4.imprint","IMPRINT",FACE,{"disambiguationData":[TD([[makeQuery(id+"F4.imprint","IMPRINT",EDGE,{"derivedFrom":sQuery(id+"F4.wireOp",EDGE,"E66.1.0.11")}),1.0]])]});
            var Q48;
            Q48=makeQuery(id+"F4.imprint","IMPRINT",FACE,{"disambiguationData":[TD([[makeQuery(id+"F4.imprint","IMPRINT",EDGE,{"derivedFrom":sQuery(id+"F4.wireOp",EDGE,"E66.1.0.38")}),1.0]])]});
            var Q49;
            Q49=makeQuery(id+"F4.imprint","IMPRINT",FACE,{"disambiguationData":[TD([[makeQuery(id+"F4.imprint","IMPRINT",EDGE,{"derivedFrom":sQuery(id+"F4.wireOp",EDGE,"E66.1.0.18")}),1.0]])]});
            var Q50;
            Q50=makeQuery(id+"F4.imprint","IMPRINT",FACE,{"disambiguationData":[TD([[makeQuery(id+"F4.imprint","IMPRINT",EDGE,{"derivedFrom":sQuery(id+"F4.wireOp",EDGE,"E66.1.0.12")}),1.0]])]});
            var Q51;
            Q51=makeQuery(id+"F4.imprint","IMPRINT",FACE,{"disambiguationData":[TD([[makeQuery(id+"F4.imprint","IMPRINT",EDGE,{"derivedFrom":sQuery(id+"F4.wireOp",EDGE,"E66.1.0.2")}),1.0]])]});
            var Q52;
            Q52=makeQuery(id+"F4.imprint","IMPRINT",FACE,{"disambiguationData":[TD([[makeQuery(id+"F4.imprint","IMPRINT",EDGE,{"derivedFrom":sQuery(id+"F4.wireOp",EDGE,"E66.1.0.17")}),-1.0]])]});
            var Q53;
            Q53=makeQuery(id+"F4.imprint","IMPRINT",FACE,{"disambiguationData":[TD([[makeQuery(id+"F4.imprint","IMPRINT",EDGE,{"derivedFrom":sQuery(id+"F4.wireOp",EDGE,"E66.1.0.41")}),1.0]])]});
            var Q54;
            Q54=makeQuery(id+"F4.imprint","IMPRINT",FACE,{"disambiguationData":[TD([[makeQuery(id+"F4.imprint","IMPRINT",EDGE,{"derivedFrom":sQuery(id+"F4.wireOp",EDGE,"E66.1.0.78")}),-1.0]])]});
            var Q55;
            Q55=makeQuery(id+"F4.imprint","IMPRINT",FACE,{"disambiguationData":[TD([[makeQuery(id+"F4.imprint","IMPRINT",EDGE,{"derivedFrom":sQuery(id+"F4.wireOp",EDGE,"E66.1.0.81")}),-1.0]])]});
            var Q56;
            Q56=makeQuery(id+"F4.imprint","IMPRINT",FACE,{"disambiguationData":[TD([[makeQuery(id+"F4.imprint","IMPRINT",EDGE,{"derivedFrom":sQuery(id+"F4.wireOp",EDGE,"E66.1.0.92")}),-1.0]])]});
            var Q57;
            Q57=makeQuery(id+"F4.imprint","IMPRINT",FACE,{"disambiguationData":[TD([[makeQuery(id+"F4.imprint","IMPRINT",EDGE,{"derivedFrom":sQuery(id+"F4.wireOp",EDGE,"E66.1.0.94")}),1.0]])]});
            var Q58;
            Q58=makeQuery(id+"F4.imprint","IMPRINT",FACE,{"disambiguationData":[TD([[makeQuery(id+"F4.imprint","IMPRINT",EDGE,{"derivedFrom":sQuery(id+"F4.wireOp",EDGE,"E66.1.0.95")}),1.0]])]});
            var Q59;
            Q59=makeQuery(id+"F4.imprint","IMPRINT",FACE,{"disambiguationData":[TD([[makeQuery(id+"F4.imprint","IMPRINT",EDGE,{"derivedFrom":sQuery(id+"F4.wireOp",EDGE,"E66.1.0.93")}),1.0]])]});
            var Q60;
            Q60=makeQuery(id+"F4.imprint","IMPRINT",FACE,{"disambiguationData":[TD([[makeQuery(id+"F4.imprint","IMPRINT",EDGE,{"derivedFrom":sQuery(id+"F4.wireOp",EDGE,"E66.4.0.25")}),1.0]])]});
            var Q61;
            Q61=makeQuery(id+"F4.imprint","IMPRINT",FACE,{"disambiguationData":[TD([[makeQuery(id+"F4.imprint","IMPRINT",EDGE,{"derivedFrom":sQuery(id+"F4.wireOp",EDGE,"E66.4.0.37")}),1.0]])]});
            var Q62;
            Q62=makeQuery(id+"F4.imprint","IMPRINT",FACE,{"disambiguationData":[TD([[makeQuery(id+"F4.imprint","IMPRINT",EDGE,{"derivedFrom":sQuery(id+"F4.wireOp",EDGE,"E66.4.0.40")}),1.0]])]});
            var Q63;
            Q63=makeQuery(id+"F4.imprint","IMPRINT",FACE,{"disambiguationData":[TD([[makeQuery(id+"F4.imprint","IMPRINT",EDGE,{"derivedFrom":sQuery(id+"F4.wireOp",EDGE,"E66.3.0.40")}),1.0]])]});
            var Q64;
            Q64=makeQuery(id+"F4.imprint","IMPRINT",FACE,{"disambiguationData":[TD([[makeQuery(id+"F4.imprint","IMPRINT",EDGE,{"derivedFrom":sQuery(id+"F4.wireOp",EDGE,"E66.3.0.37")}),1.0]])]});
            var Q65;
            Q65=makeQuery(id+"F4.imprint","IMPRINT",FACE,{"disambiguationData":[TD([[makeQuery(id+"F4.imprint","IMPRINT",EDGE,{"derivedFrom":sQuery(id+"F4.wireOp",EDGE,"E66.2.0.40")}),1.0]])]});
            extrude(context, id + "F5", {"entities" : qUnion([Q0, Q1, Q2, Q3, Q4, Q5, Q6, Q7, Q8, Q9, Q10, Q11, Q12, Q13, Q14, Q15, Q16, Q17, Q18, Q19, Q20, Q21, Q22, Q23, Q24, Q25, Q26, Q27, Q28, Q29, Q30, Q31, Q32, Q33, Q34, Q35, Q36, Q37, Q38, Q39, Q40, Q41, Q42, Q43, Q44, Q45, Q46, Q47, Q48, Q49, Q50, Q51, Q52, Q53, Q54, Q55, Q56, Q57, Q58, Q59, Q60, Q61, Q62, Q63, Q64, Q65]), "operationType" : NewBodyOperationType.ADD, "depth" : 0.8 * mm, "offsetDistance" : 25.4 * mm});
        }
        {
            var Q0;
            Q0=makeQuery(id+"F1.opExtrude","CAP_FACE",FACE,{"disambiguationData":[OSD([sQuery(id+"F0.wireOp",EDGE,"E0.bottom"),sQuery(id+"F0.wireOp",EDGE,"E0.top"),sQuery(id+"F0.wireOp",EDGE,"E0.left"),sQuery(id+"F0.wireOp",EDGE,"E0.right")])],"isStart":false});
            var sketch = newSketch(context, id + "F6", { "sketchPlane" : qUnion([Q0])});
            skText(sketch, "E188", { "text": "Christian", "fontName": "AllertaStencil-Regular.ttf"});
            skText(sketch, "E189", { "text": "Vision", "fontName": "AllertaStencil-Regular.ttf"});
            skText(sketch, "E190", { "text": "Team 501", "fontName": "AllertaStencil-Regular.ttf"});
            skPoint(sketch, "E191", {"position": v(0, 2.54) * mm});
            skPoint(sketch, "E192", {"position": v(0, 0) * mm});
            const initialGuessF6  = {"E188": [-0.03937, 0.0127, 1, 0, 0.00762], "E189": [0.01826, 0.00508, 1, 0, 0.00508], "E190": [-0.01668, -0.00254, 1, 0, 0.00508]};
            skSetInitialGuess(sketch, initialGuessF6);
            skSolve(sketch);
        }
        {
            var Q0;
            Q0=qSketchRegion(id+"F6",true);
            extrude(context, id + "F7", {"entities" : qUnion([Q0]), "operationType" : NewBodyOperationType.REMOVE, "oppositeDirection" : true, "depth" : 1 / 812.8 * mm, "offsetDistance" : 25.4 * mm, "hasSecondDirection" : true, "secondDirectionOppositeDirection" : false, "secondDirectionDepth" : 25.4 * mm});
        }
        {
            var Q0;
            Q0=makeQuery(id+"F1.opExtrude","SWEPT_EDGE",EDGE,{"disambiguationData":[OSD([sQuery(id+"F0.wireOp",EDGE,"E0.bottom"),sQuery(id+"F0.wireOp",EDGE,"E0.left")])]});
            var Q1;
            Q1=makeQuery(id+"F1.opExtrude","SWEPT_EDGE",EDGE,{"disambiguationData":[OSD([sQuery(id+"F0.wireOp",EDGE,"E0.bottom"),sQuery(id+"F0.wireOp",EDGE,"E0.right")])]});
            var Q2;
            Q2=makeQuery(id+"F1.opExtrude","SWEPT_EDGE",EDGE,{"disambiguationData":[OSD([sQuery(id+"F0.wireOp",EDGE,"E0.top"),sQuery(id+"F0.wireOp",EDGE,"E0.right")])]});
            var Q3;
            Q3=makeQuery(id+"F1.opExtrude","SWEPT_EDGE",EDGE,{"disambiguationData":[OSD([sQuery(id+"F0.wireOp",EDGE,"E0.top"),sQuery(id+"F0.wireOp",EDGE,"E0.left")])]});
            fillet(context, id + "F8", {"entities" : qUnion([Q0, Q1, Q2, Q3]), "radius" : 5.08 * mm, "tangentPropagation" : true, "allowEdgeOverflow" : false});
        }
        {
            var Q0;
            Q0=makeQuery(id+"F1.opExtrude","CAP_EDGE",EDGE,{"disambiguationData":[OSD([sQuery(id+"F0.wireOp",EDGE,"E0.bottom")])],"isStart":false});
            fillet(context, id + "F9", {"entities" : qUnion([Q0]), "radius" : 5.08 * mm, "tangentPropagation" : true, "allowEdgeOverflow" : false});
        }
    });
